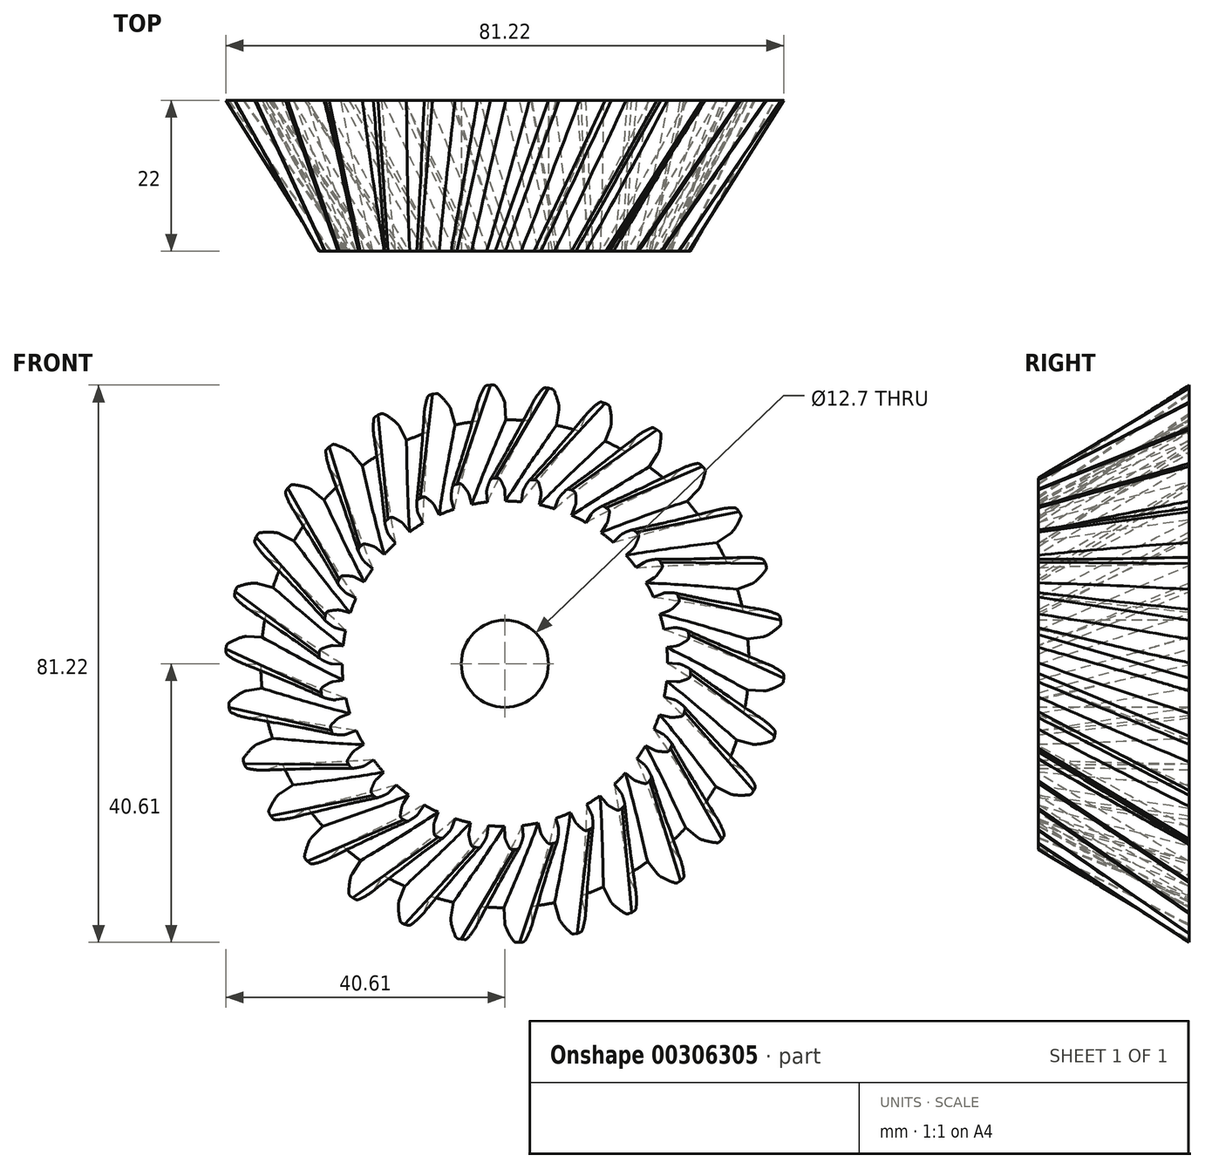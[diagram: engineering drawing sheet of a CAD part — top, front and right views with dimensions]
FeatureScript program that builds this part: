
annotation { "Feature Type Name" : "Feature", "Feature Type Description" : "" }
export const myFeature = defineFeature(function(context is Context, id is Id, definition is map)
    precondition{}
    {
        {
            var Q0;
            Q0=qCreatedBy(makeId("Front.planeOp"),FACE);
            var sketch = newSketch(context, id + "F0", { "sketchPlane" : qUnion([Q0])});
            skCircle(sketch, "E0", {"center": v(0, 0) * mm, "radius": 35.56 * mm});
            skPoint(sketch, "E1.endSnap0", {"position": v(-2, 38.15) * mm});
            skArc(sketch, "E2.trimOffspring", {"start": v(-0.1, 38.37) * mm, "mid": v(-0.63, 39.43) * mm, "end": v(-1.28, 40.41) * mm});
            skLineSegment(sketch, "E3", {"start": v(0.01, 37.84) * mm, "end": v(0.13, 35.56) * mm});
            skLineSegment(sketch, "E4", {"start": v(-1.68, 40.61) * mm, "end": v(-2.13, 40.61) * mm});
            skLineSegment(sketch, "E5.MirrorCS", {"start": v(-2.57, 40.57) * mm, "end": v(-2.13, 40.61) * mm});
            skArc(sketch, "E6.MirrorCS", {"start": v(-3.9, 38.17) * mm, "mid": v(-3.5, 39.27) * mm, "end": v(-2.96, 40.32) * mm});
            skLineSegment(sketch, "E7.MirrorCS", {"start": v(-3.97, 37.63) * mm, "end": v(-3.85, 35.35) * mm});
            skPoint(sketch, "E8.visualSharp", {"position": v(-2.82, 40.54) * mm});
            skArc(sketch, "E8.filletArc", {"start": v(-2.57, 40.57) * mm, "mid": v(-2.8, 40.5) * mm, "end": v(-2.96, 40.32) * mm});
            skPoint(sketch, "E9.visualSharp", {"position": v(-1.43, 40.61) * mm});
            skArc(sketch, "E9.filletArc", {"start": v(-1.28, 40.41) * mm, "mid": v(-1.45, 40.56) * mm, "end": v(-1.68, 40.61) * mm});
            skPoint(sketch, "E10.visualSharp", {"position": v(-3.98, 37.9) * mm});
            skArc(sketch, "E10.filletArc", {"start": v(-3.9, 38.17) * mm, "mid": v(-3.96, 37.9) * mm, "end": v(-3.97, 37.63) * mm});
            skPoint(sketch, "E11.visualSharp", {"position": v(0, 38.1) * mm});
            skArc(sketch, "E11.filletArc", {"start": v(0.01, 37.84) * mm, "mid": v(-0.02, 38.1) * mm, "end": v(-0.1, 38.37) * mm});
            skLineSegment(sketch, "E12.1.0", {"start": v(-11.7, 35.98) * mm, "end": v(-11.12, 33.78) * mm});
            skArc(sketch, "E12.1.1", {"start": v(-11.75, 36.52) * mm, "mid": v(-11.75, 36.25) * mm, "end": v(-11.7, 35.98) * mm});
            skArc(sketch, "E12.1.2", {"start": v(-11.75, 36.52) * mm, "mid": v(-11.59, 37.69) * mm, "end": v(-11.27, 38.83) * mm});
            skArc(sketch, "E12.1.3", {"start": v(-10.95, 39.15) * mm, "mid": v(-11.15, 39.03) * mm, "end": v(-11.27, 38.83) * mm});
            skLineSegment(sketch, "E12.1.4", {"start": v(-10.95, 39.15) * mm, "end": v(-10.53, 39.28) * mm});
            skLineSegment(sketch, "E12.1.5", {"start": v(-10.09, 39.38) * mm, "end": v(-10.53, 39.28) * mm});
            skArc(sketch, "E12.1.6", {"start": v(-9.65, 39.26) * mm, "mid": v(-9.86, 39.37) * mm, "end": v(-10.09, 39.38) * mm});
            skArc(sketch, "E12.1.7", {"start": v(-8.08, 37.5) * mm, "mid": v(-8.81, 38.43) * mm, "end": v(-9.65, 39.26) * mm});
            skArc(sketch, "E12.1.8", {"start": v(-7.85, 37.01) * mm, "mid": v(-7.95, 37.27) * mm, "end": v(-8.08, 37.5) * mm});
            skLineSegment(sketch, "E12.1.9", {"start": v(-7.85, 37.01) * mm, "end": v(-7.26, 34.81) * mm});
            skLineSegment(sketch, "E12.2.0", {"start": v(-18.93, 32.76) * mm, "end": v(-17.9, 30.73) * mm});
            skArc(sketch, "E12.2.1", {"start": v(-19.1, 33.28) * mm, "mid": v(-19.03, 33.01) * mm, "end": v(-18.93, 32.76) * mm});
            skArc(sketch, "E12.2.2", {"start": v(-19.1, 33.28) * mm, "mid": v(-19.17, 34.46) * mm, "end": v(-19.1, 35.64) * mm});
            skArc(sketch, "E12.2.3", {"start": v(-18.85, 36.01) * mm, "mid": v(-19.02, 35.85) * mm, "end": v(-19.1, 35.64) * mm});
            skLineSegment(sketch, "E12.2.4", {"start": v(-18.85, 36.01) * mm, "end": v(-18.46, 36.24) * mm});
            skLineSegment(sketch, "E12.2.5", {"start": v(-18.06, 36.42) * mm, "end": v(-18.46, 36.24) * mm});
            skArc(sketch, "E12.2.6", {"start": v(-17.6, 36.4) * mm, "mid": v(-17.83, 36.46) * mm, "end": v(-18.06, 36.42) * mm});
            skArc(sketch, "E12.2.7", {"start": v(-15.7, 35) * mm, "mid": v(-16.6, 35.76) * mm, "end": v(-17.6, 36.4) * mm});
            skArc(sketch, "E12.2.8", {"start": v(-15.38, 34.57) * mm, "mid": v(-15.52, 34.8) * mm, "end": v(-15.7, 35) * mm});
            skLineSegment(sketch, "E12.2.9", {"start": v(-15.38, 34.57) * mm, "end": v(-14.34, 32.54) * mm});
            skLineSegment(sketch, "E12.3.0", {"start": v(-25.33, 28.11) * mm, "end": v(-23.9, 26.34) * mm});
            skArc(sketch, "E12.3.1", {"start": v(-25.6, 28.58) * mm, "mid": v(-25.48, 28.34) * mm, "end": v(-25.33, 28.11) * mm});
            skArc(sketch, "E12.3.2", {"start": v(-25.6, 28.58) * mm, "mid": v(-25.91, 29.72) * mm, "end": v(-26.1, 30.88) * mm});
            skArc(sketch, "E12.3.3", {"start": v(-25.93, 31.3) * mm, "mid": v(-26.06, 31.12) * mm, "end": v(-26.1, 30.88) * mm});
            skLineSegment(sketch, "E12.3.4", {"start": v(-25.93, 31.3) * mm, "end": v(-25.6, 31.6) * mm});
            skLineSegment(sketch, "E12.3.5", {"start": v(-25.23, 31.87) * mm, "end": v(-25.6, 31.6) * mm});
            skArc(sketch, "E12.3.6", {"start": v(-24.79, 31.94) * mm, "mid": v(-25.02, 31.96) * mm, "end": v(-25.23, 31.87) * mm});
            skArc(sketch, "E12.3.7", {"start": v(-22.64, 30.98) * mm, "mid": v(-23.68, 31.53) * mm, "end": v(-24.79, 31.94) * mm});
            skArc(sketch, "E12.3.8", {"start": v(-22.23, 30.62) * mm, "mid": v(-22.42, 30.82) * mm, "end": v(-22.64, 30.98) * mm});
            skLineSegment(sketch, "E12.3.9", {"start": v(-22.23, 30.62) * mm, "end": v(-20.8, 28.85) * mm});
            skLineSegment(sketch, "E12.4.0", {"start": v(-30.62, 22.23) * mm, "end": v(-28.85, 20.8) * mm});
            skArc(sketch, "E12.4.1", {"start": v(-30.98, 22.64) * mm, "mid": v(-30.82, 22.42) * mm, "end": v(-30.62, 22.23) * mm});
            skArc(sketch, "E12.4.2", {"start": v(-30.98, 22.64) * mm, "mid": v(-31.53, 23.68) * mm, "end": v(-31.94, 24.79) * mm});
            skArc(sketch, "E12.4.3", {"start": v(-31.87, 25.23) * mm, "mid": v(-31.96, 25.02) * mm, "end": v(-31.94, 24.79) * mm});
            skLineSegment(sketch, "E12.4.4", {"start": v(-31.87, 25.23) * mm, "end": v(-31.6, 25.6) * mm});
            skLineSegment(sketch, "E12.4.5", {"start": v(-31.3, 25.93) * mm, "end": v(-31.6, 25.6) * mm});
            skArc(sketch, "E12.4.6", {"start": v(-30.88, 26.1) * mm, "mid": v(-31.12, 26.06) * mm, "end": v(-31.3, 25.93) * mm});
            skArc(sketch, "E12.4.7", {"start": v(-28.58, 25.6) * mm, "mid": v(-29.72, 25.91) * mm, "end": v(-30.88, 26.1) * mm});
            skArc(sketch, "E12.4.8", {"start": v(-28.11, 25.33) * mm, "mid": v(-28.34, 25.48) * mm, "end": v(-28.58, 25.6) * mm});
            skLineSegment(sketch, "E12.4.9", {"start": v(-28.11, 25.33) * mm, "end": v(-26.34, 23.9) * mm});
            skLineSegment(sketch, "E12.5.0", {"start": v(-34.57, 15.38) * mm, "end": v(-32.54, 14.34) * mm});
            skArc(sketch, "E12.5.1", {"start": v(-35, 15.7) * mm, "mid": v(-34.8, 15.52) * mm, "end": v(-34.57, 15.38) * mm});
            skArc(sketch, "E12.5.2", {"start": v(-35, 15.7) * mm, "mid": v(-35.76, 16.6) * mm, "end": v(-36.4, 17.6) * mm});
            skArc(sketch, "E12.5.3", {"start": v(-36.42, 18.06) * mm, "mid": v(-36.46, 17.83) * mm, "end": v(-36.4, 17.6) * mm});
            skLineSegment(sketch, "E12.5.4", {"start": v(-36.42, 18.06) * mm, "end": v(-36.24, 18.46) * mm});
            skLineSegment(sketch, "E12.5.5", {"start": v(-36.01, 18.85) * mm, "end": v(-36.24, 18.46) * mm});
            skArc(sketch, "E12.5.6", {"start": v(-35.64, 19.1) * mm, "mid": v(-35.85, 19.02) * mm, "end": v(-36.01, 18.85) * mm});
            skArc(sketch, "E12.5.7", {"start": v(-33.28, 19.1) * mm, "mid": v(-34.46, 19.17) * mm, "end": v(-35.64, 19.1) * mm});
            skArc(sketch, "E12.5.8", {"start": v(-32.76, 18.93) * mm, "mid": v(-33.01, 19.03) * mm, "end": v(-33.28, 19.1) * mm});
            skLineSegment(sketch, "E12.5.9", {"start": v(-32.76, 18.93) * mm, "end": v(-30.73, 17.9) * mm});
            skLineSegment(sketch, "E12.6.0", {"start": v(-37.01, 7.85) * mm, "end": v(-34.81, 7.26) * mm});
            skArc(sketch, "E12.6.1", {"start": v(-37.5, 8.08) * mm, "mid": v(-37.27, 7.95) * mm, "end": v(-37.01, 7.85) * mm});
            skArc(sketch, "E12.6.2", {"start": v(-37.5, 8.08) * mm, "mid": v(-38.43, 8.81) * mm, "end": v(-39.26, 9.65) * mm});
            skArc(sketch, "E12.6.3", {"start": v(-39.38, 10.09) * mm, "mid": v(-39.37, 9.86) * mm, "end": v(-39.26, 9.65) * mm});
            skLineSegment(sketch, "E12.6.4", {"start": v(-39.38, 10.09) * mm, "end": v(-39.28, 10.53) * mm});
            skLineSegment(sketch, "E12.6.5", {"start": v(-39.15, 10.95) * mm, "end": v(-39.28, 10.53) * mm});
            skArc(sketch, "E12.6.6", {"start": v(-38.83, 11.27) * mm, "mid": v(-39.03, 11.15) * mm, "end": v(-39.15, 10.95) * mm});
            skArc(sketch, "E12.6.7", {"start": v(-36.52, 11.75) * mm, "mid": v(-37.69, 11.59) * mm, "end": v(-38.83, 11.27) * mm});
            skArc(sketch, "E12.6.8", {"start": v(-35.98, 11.7) * mm, "mid": v(-36.25, 11.75) * mm, "end": v(-36.52, 11.75) * mm});
            skLineSegment(sketch, "E12.6.9", {"start": v(-35.98, 11.7) * mm, "end": v(-33.78, 11.12) * mm});
            skLineSegment(sketch, "E12.7.0", {"start": v(-37.84, -0.01) * mm, "end": v(-35.56, -0.13) * mm});
            skArc(sketch, "E12.7.1", {"start": v(-38.37, 0.1) * mm, "mid": v(-38.1, 0.02) * mm, "end": v(-37.84, -0.01) * mm});
            skArc(sketch, "E12.7.2", {"start": v(-38.37, 0.1) * mm, "mid": v(-39.43, 0.63) * mm, "end": v(-40.41, 1.28) * mm});
            skArc(sketch, "E12.7.3", {"start": v(-40.61, 1.68) * mm, "mid": v(-40.56, 1.45) * mm, "end": v(-40.41, 1.28) * mm});
            skLineSegment(sketch, "E12.7.4", {"start": v(-40.61, 1.68) * mm, "end": v(-40.61, 2.13) * mm});
            skLineSegment(sketch, "E12.7.5", {"start": v(-40.57, 2.57) * mm, "end": v(-40.61, 2.13) * mm});
            skArc(sketch, "E12.7.6", {"start": v(-40.32, 2.96) * mm, "mid": v(-40.5, 2.8) * mm, "end": v(-40.57, 2.57) * mm});
            skArc(sketch, "E12.7.7", {"start": v(-38.17, 3.9) * mm, "mid": v(-39.27, 3.5) * mm, "end": v(-40.32, 2.96) * mm});
            skArc(sketch, "E12.7.8", {"start": v(-37.63, 3.97) * mm, "mid": v(-37.9, 3.96) * mm, "end": v(-38.17, 3.9) * mm});
            skLineSegment(sketch, "E12.7.9", {"start": v(-37.63, 3.97) * mm, "end": v(-35.35, 3.85) * mm});
            skLineSegment(sketch, "E12.8.0", {"start": v(-37, -7.88) * mm, "end": v(-34.76, -7.52) * mm});
            skArc(sketch, "E12.8.1", {"start": v(-37.55, -7.87) * mm, "mid": v(-37.28, -7.9) * mm, "end": v(-37, -7.88) * mm});
            skArc(sketch, "E12.8.2", {"start": v(-37.55, -7.87) * mm, "mid": v(-38.7, -7.58) * mm, "end": v(-39.8, -7.15) * mm});
            skArc(sketch, "E12.8.3", {"start": v(-40.08, -6.8) * mm, "mid": v(-39.98, -7.01) * mm, "end": v(-39.8, -7.15) * mm});
            skLineSegment(sketch, "E12.8.4", {"start": v(-40.08, -6.8) * mm, "end": v(-40.17, -6.36) * mm});
            skLineSegment(sketch, "E12.8.5", {"start": v(-40.22, -5.92) * mm, "end": v(-40.17, -6.36) * mm});
            skArc(sketch, "E12.8.6", {"start": v(-40.06, -5.5) * mm, "mid": v(-40.19, -5.69) * mm, "end": v(-40.22, -5.92) * mm});
            skArc(sketch, "E12.8.7", {"start": v(-38.15, -4.12) * mm, "mid": v(-39.14, -4.75) * mm, "end": v(-40.06, -5.5) * mm});
            skArc(sketch, "E12.8.8", {"start": v(-37.63, -3.94) * mm, "mid": v(-37.9, -4) * mm, "end": v(-38.15, -4.12) * mm});
            skLineSegment(sketch, "E12.8.9", {"start": v(-37.63, -3.94) * mm, "end": v(-35.38, -3.58) * mm});
            skLineSegment(sketch, "E12.9.0", {"start": v(-34.56, -15.4) * mm, "end": v(-32.43, -14.59) * mm});
            skArc(sketch, "E12.9.1", {"start": v(-35.1, -15.5) * mm, "mid": v(-34.82, -15.48) * mm, "end": v(-34.56, -15.4) * mm});
            skArc(sketch, "E12.9.2", {"start": v(-35.1, -15.5) * mm, "mid": v(-36.27, -15.46) * mm, "end": v(-37.44, -15.27) * mm});
            skArc(sketch, "E12.9.3", {"start": v(-37.79, -14.98) * mm, "mid": v(-37.65, -15.17) * mm, "end": v(-37.44, -15.27) * mm});
            skLineSegment(sketch, "E12.9.4", {"start": v(-37.79, -14.98) * mm, "end": v(-37.97, -14.58) * mm});
            skLineSegment(sketch, "E12.9.5", {"start": v(-38.1, -14.15) * mm, "end": v(-37.97, -14.58) * mm});
            skArc(sketch, "E12.9.6", {"start": v(-38.04, -13.7) * mm, "mid": v(-38.13, -13.92) * mm, "end": v(-38.1, -14.15) * mm});
            skArc(sketch, "E12.9.7", {"start": v(-36.46, -11.96) * mm, "mid": v(-37.3, -12.78) * mm, "end": v(-38.04, -13.7) * mm});
            skArc(sketch, "E12.9.8", {"start": v(-36, -11.68) * mm, "mid": v(-36.24, -11.8) * mm, "end": v(-36.46, -11.96) * mm});
            skLineSegment(sketch, "E12.9.9", {"start": v(-36, -11.68) * mm, "end": v(-33.86, -10.86) * mm});
            skLineSegment(sketch, "E12.10.0", {"start": v(-30.6, -22.25) * mm, "end": v(-28.7, -21) * mm});
            skArc(sketch, "E12.10.1", {"start": v(-31.1, -22.47) * mm, "mid": v(-30.84, -22.38) * mm, "end": v(-30.6, -22.25) * mm});
            skArc(sketch, "E12.10.2", {"start": v(-31.1, -22.47) * mm, "mid": v(-32.26, -22.67) * mm, "end": v(-33.44, -22.72) * mm});
            skArc(sketch, "E12.10.3", {"start": v(-33.85, -22.51) * mm, "mid": v(-33.67, -22.66) * mm, "end": v(-33.44, -22.72) * mm});
            skLineSegment(sketch, "E12.10.4", {"start": v(-33.85, -22.51) * mm, "end": v(-34.1, -22.15) * mm});
            skLineSegment(sketch, "E12.10.5", {"start": v(-34.33, -21.76) * mm, "end": v(-34.1, -22.15) * mm});
            skArc(sketch, "E12.10.6", {"start": v(-34.36, -21.31) * mm, "mid": v(-34.4, -21.54) * mm, "end": v(-34.33, -21.76) * mm});
            skArc(sketch, "E12.10.7", {"start": v(-33.17, -19.28) * mm, "mid": v(-33.83, -20.26) * mm, "end": v(-34.36, -21.31) * mm});
            skArc(sketch, "E12.10.8", {"start": v(-32.78, -18.9) * mm, "mid": v(-33, -19.07) * mm, "end": v(-33.17, -19.28) * mm});
            skLineSegment(sketch, "E12.10.9", {"start": v(-32.78, -18.9) * mm, "end": v(-30.86, -17.66) * mm});
            skLineSegment(sketch, "E12.11.0", {"start": v(-25.3, -28.13) * mm, "end": v(-23.7, -26.52) * mm});
            skArc(sketch, "E12.11.1", {"start": v(-25.75, -28.44) * mm, "mid": v(-25.52, -28.3) * mm, "end": v(-25.3, -28.13) * mm});
            skArc(sketch, "E12.11.2", {"start": v(-25.75, -28.44) * mm, "mid": v(-26.85, -28.88) * mm, "end": v(-27.99, -29.18) * mm});
            skArc(sketch, "E12.11.3", {"start": v(-28.43, -29.06) * mm, "mid": v(-28.22, -29.17) * mm, "end": v(-27.99, -29.18) * mm});
            skLineSegment(sketch, "E12.11.4", {"start": v(-28.43, -29.06) * mm, "end": v(-28.76, -28.76) * mm});
            skLineSegment(sketch, "E12.11.5", {"start": v(-29.06, -28.43) * mm, "end": v(-28.76, -28.76) * mm});
            skArc(sketch, "E12.11.6", {"start": v(-29.18, -27.99) * mm, "mid": v(-29.17, -28.22) * mm, "end": v(-29.06, -28.43) * mm});
            skArc(sketch, "E12.11.7", {"start": v(-28.44, -25.75) * mm, "mid": v(-28.88, -26.85) * mm, "end": v(-29.18, -27.99) * mm});
            skArc(sketch, "E12.11.8", {"start": v(-28.13, -25.3) * mm, "mid": v(-28.3, -25.52) * mm, "end": v(-28.44, -25.75) * mm});
            skLineSegment(sketch, "E12.11.9", {"start": v(-28.13, -25.3) * mm, "end": v(-26.52, -23.7) * mm});
            skLineSegment(sketch, "E12.12.0", {"start": v(-18.9, -32.78) * mm, "end": v(-17.66, -30.86) * mm});
            skArc(sketch, "E12.12.1", {"start": v(-19.28, -33.17) * mm, "mid": v(-19.07, -33) * mm, "end": v(-18.9, -32.78) * mm});
            skArc(sketch, "E12.12.2", {"start": v(-19.28, -33.17) * mm, "mid": v(-20.26, -33.83) * mm, "end": v(-21.31, -34.36) * mm});
            skArc(sketch, "E12.12.3", {"start": v(-21.76, -34.33) * mm, "mid": v(-21.54, -34.4) * mm, "end": v(-21.31, -34.36) * mm});
            skLineSegment(sketch, "E12.12.4", {"start": v(-21.76, -34.33) * mm, "end": v(-22.15, -34.1) * mm});
            skLineSegment(sketch, "E12.12.5", {"start": v(-22.51, -33.85) * mm, "end": v(-22.15, -34.1) * mm});
            skArc(sketch, "E12.12.6", {"start": v(-22.72, -33.44) * mm, "mid": v(-22.66, -33.67) * mm, "end": v(-22.51, -33.85) * mm});
            skArc(sketch, "E12.12.7", {"start": v(-22.47, -31.1) * mm, "mid": v(-22.67, -32.26) * mm, "end": v(-22.72, -33.44) * mm});
            skArc(sketch, "E12.12.8", {"start": v(-22.25, -30.6) * mm, "mid": v(-22.38, -30.84) * mm, "end": v(-22.47, -31.1) * mm});
            skLineSegment(sketch, "E12.12.9", {"start": v(-22.25, -30.6) * mm, "end": v(-21, -28.7) * mm});
            skLineSegment(sketch, "E12.13.0", {"start": v(-11.68, -36) * mm, "end": v(-10.86, -33.86) * mm});
            skArc(sketch, "E12.13.1", {"start": v(-11.96, -36.46) * mm, "mid": v(-11.8, -36.24) * mm, "end": v(-11.68, -36) * mm});
            skArc(sketch, "E12.13.2", {"start": v(-11.96, -36.46) * mm, "mid": v(-12.78, -37.3) * mm, "end": v(-13.7, -38.04) * mm});
            skArc(sketch, "E12.13.3", {"start": v(-14.15, -38.1) * mm, "mid": v(-13.92, -38.13) * mm, "end": v(-13.7, -38.04) * mm});
            skLineSegment(sketch, "E12.13.4", {"start": v(-14.15, -38.1) * mm, "end": v(-14.58, -37.97) * mm});
            skLineSegment(sketch, "E12.13.5", {"start": v(-14.98, -37.79) * mm, "end": v(-14.58, -37.97) * mm});
            skArc(sketch, "E12.13.6", {"start": v(-15.27, -37.44) * mm, "mid": v(-15.17, -37.65) * mm, "end": v(-14.98, -37.79) * mm});
            skArc(sketch, "E12.13.7", {"start": v(-15.5, -35.1) * mm, "mid": v(-15.46, -36.27) * mm, "end": v(-15.27, -37.44) * mm});
            skArc(sketch, "E12.13.8", {"start": v(-15.4, -34.56) * mm, "mid": v(-15.48, -34.82) * mm, "end": v(-15.5, -35.1) * mm});
            skLineSegment(sketch, "E12.13.9", {"start": v(-15.4, -34.56) * mm, "end": v(-14.59, -32.43) * mm});
            skLineSegment(sketch, "E12.14.0", {"start": v(-3.94, -37.63) * mm, "end": v(-3.58, -35.38) * mm});
            skArc(sketch, "E12.14.1", {"start": v(-4.12, -38.15) * mm, "mid": v(-4, -37.9) * mm, "end": v(-3.94, -37.63) * mm});
            skArc(sketch, "E12.14.2", {"start": v(-4.12, -38.15) * mm, "mid": v(-4.75, -39.14) * mm, "end": v(-5.5, -40.06) * mm});
            skArc(sketch, "E12.14.3", {"start": v(-5.92, -40.22) * mm, "mid": v(-5.69, -40.19) * mm, "end": v(-5.5, -40.06) * mm});
            skLineSegment(sketch, "E12.14.4", {"start": v(-5.92, -40.22) * mm, "end": v(-6.36, -40.17) * mm});
            skLineSegment(sketch, "E12.14.5", {"start": v(-6.8, -40.08) * mm, "end": v(-6.36, -40.17) * mm});
            skArc(sketch, "E12.14.6", {"start": v(-7.15, -39.8) * mm, "mid": v(-7.01, -39.98) * mm, "end": v(-6.8, -40.08) * mm});
            skArc(sketch, "E12.14.7", {"start": v(-7.87, -37.55) * mm, "mid": v(-7.58, -38.7) * mm, "end": v(-7.15, -39.8) * mm});
            skArc(sketch, "E12.14.8", {"start": v(-7.88, -37) * mm, "mid": v(-7.9, -37.28) * mm, "end": v(-7.87, -37.55) * mm});
            skLineSegment(sketch, "E12.14.9", {"start": v(-7.88, -37) * mm, "end": v(-7.52, -34.76) * mm});
            skLineSegment(sketch, "E12.15.0", {"start": v(3.97, -37.63) * mm, "end": v(3.85, -35.35) * mm});
            skArc(sketch, "E12.15.1", {"start": v(3.9, -38.17) * mm, "mid": v(3.96, -37.9) * mm, "end": v(3.97, -37.63) * mm});
            skArc(sketch, "E12.15.2", {"start": v(3.9, -38.17) * mm, "mid": v(3.5, -39.27) * mm, "end": v(2.96, -40.32) * mm});
            skArc(sketch, "E12.15.3", {"start": v(2.57, -40.57) * mm, "mid": v(2.8, -40.5) * mm, "end": v(2.96, -40.32) * mm});
            skLineSegment(sketch, "E12.15.4", {"start": v(2.57, -40.57) * mm, "end": v(2.13, -40.61) * mm});
            skLineSegment(sketch, "E12.15.5", {"start": v(1.68, -40.61) * mm, "end": v(2.13, -40.61) * mm});
            skArc(sketch, "E12.15.6", {"start": v(1.28, -40.41) * mm, "mid": v(1.45, -40.56) * mm, "end": v(1.68, -40.61) * mm});
            skArc(sketch, "E12.15.7", {"start": v(0.1, -38.37) * mm, "mid": v(0.63, -39.43) * mm, "end": v(1.28, -40.41) * mm});
            skArc(sketch, "E12.15.8", {"start": v(-0.01, -37.84) * mm, "mid": v(0.02, -38.1) * mm, "end": v(0.1, -38.37) * mm});
            skLineSegment(sketch, "E12.15.9", {"start": v(-0.01, -37.84) * mm, "end": v(-0.13, -35.56) * mm});
            skLineSegment(sketch, "E12.16.0", {"start": v(11.7, -35.98) * mm, "end": v(11.12, -33.78) * mm});
            skArc(sketch, "E12.16.1", {"start": v(11.75, -36.52) * mm, "mid": v(11.75, -36.25) * mm, "end": v(11.7, -35.98) * mm});
            skArc(sketch, "E12.16.2", {"start": v(11.75, -36.52) * mm, "mid": v(11.59, -37.69) * mm, "end": v(11.27, -38.83) * mm});
            skArc(sketch, "E12.16.3", {"start": v(10.95, -39.15) * mm, "mid": v(11.15, -39.03) * mm, "end": v(11.27, -38.83) * mm});
            skLineSegment(sketch, "E12.16.4", {"start": v(10.95, -39.15) * mm, "end": v(10.53, -39.28) * mm});
            skLineSegment(sketch, "E12.16.5", {"start": v(10.09, -39.38) * mm, "end": v(10.53, -39.28) * mm});
            skArc(sketch, "E12.16.6", {"start": v(9.65, -39.26) * mm, "mid": v(9.86, -39.37) * mm, "end": v(10.09, -39.38) * mm});
            skArc(sketch, "E12.16.7", {"start": v(8.08, -37.5) * mm, "mid": v(8.81, -38.43) * mm, "end": v(9.65, -39.26) * mm});
            skArc(sketch, "E12.16.8", {"start": v(7.85, -37.01) * mm, "mid": v(7.95, -37.27) * mm, "end": v(8.08, -37.5) * mm});
            skLineSegment(sketch, "E12.16.9", {"start": v(7.85, -37.01) * mm, "end": v(7.26, -34.81) * mm});
            skLineSegment(sketch, "E12.17.0", {"start": v(18.93, -32.76) * mm, "end": v(17.9, -30.73) * mm});
            skArc(sketch, "E12.17.1", {"start": v(19.1, -33.28) * mm, "mid": v(19.03, -33.01) * mm, "end": v(18.93, -32.76) * mm});
            skArc(sketch, "E12.17.2", {"start": v(19.1, -33.28) * mm, "mid": v(19.17, -34.46) * mm, "end": v(19.1, -35.64) * mm});
            skArc(sketch, "E12.17.3", {"start": v(18.85, -36.01) * mm, "mid": v(19.02, -35.85) * mm, "end": v(19.1, -35.64) * mm});
            skLineSegment(sketch, "E12.17.4", {"start": v(18.85, -36.01) * mm, "end": v(18.46, -36.24) * mm});
            skLineSegment(sketch, "E12.17.5", {"start": v(18.06, -36.42) * mm, "end": v(18.46, -36.24) * mm});
            skArc(sketch, "E12.17.6", {"start": v(17.6, -36.4) * mm, "mid": v(17.83, -36.46) * mm, "end": v(18.06, -36.42) * mm});
            skArc(sketch, "E12.17.7", {"start": v(15.7, -35) * mm, "mid": v(16.6, -35.76) * mm, "end": v(17.6, -36.4) * mm});
            skArc(sketch, "E12.17.8", {"start": v(15.38, -34.57) * mm, "mid": v(15.52, -34.8) * mm, "end": v(15.7, -35) * mm});
            skLineSegment(sketch, "E12.17.9", {"start": v(15.38, -34.57) * mm, "end": v(14.34, -32.54) * mm});
            skLineSegment(sketch, "E12.18.0", {"start": v(25.33, -28.11) * mm, "end": v(23.9, -26.34) * mm});
            skArc(sketch, "E12.18.1", {"start": v(25.6, -28.58) * mm, "mid": v(25.48, -28.34) * mm, "end": v(25.33, -28.11) * mm});
            skArc(sketch, "E12.18.2", {"start": v(25.6, -28.58) * mm, "mid": v(25.91, -29.72) * mm, "end": v(26.1, -30.88) * mm});
            skArc(sketch, "E12.18.3", {"start": v(25.93, -31.3) * mm, "mid": v(26.06, -31.12) * mm, "end": v(26.1, -30.88) * mm});
            skLineSegment(sketch, "E12.18.4", {"start": v(25.93, -31.3) * mm, "end": v(25.6, -31.6) * mm});
            skLineSegment(sketch, "E12.18.5", {"start": v(25.23, -31.87) * mm, "end": v(25.6, -31.6) * mm});
            skArc(sketch, "E12.18.6", {"start": v(24.79, -31.94) * mm, "mid": v(25.02, -31.96) * mm, "end": v(25.23, -31.87) * mm});
            skArc(sketch, "E12.18.7", {"start": v(22.64, -30.98) * mm, "mid": v(23.68, -31.53) * mm, "end": v(24.79, -31.94) * mm});
            skArc(sketch, "E12.18.8", {"start": v(22.23, -30.62) * mm, "mid": v(22.42, -30.82) * mm, "end": v(22.64, -30.98) * mm});
            skLineSegment(sketch, "E12.18.9", {"start": v(22.23, -30.62) * mm, "end": v(20.8, -28.85) * mm});
            skLineSegment(sketch, "E12.19.0", {"start": v(30.62, -22.23) * mm, "end": v(28.85, -20.8) * mm});
            skArc(sketch, "E12.19.1", {"start": v(30.98, -22.64) * mm, "mid": v(30.82, -22.42) * mm, "end": v(30.62, -22.23) * mm});
            skArc(sketch, "E12.19.2", {"start": v(30.98, -22.64) * mm, "mid": v(31.53, -23.68) * mm, "end": v(31.94, -24.79) * mm});
            skArc(sketch, "E12.19.3", {"start": v(31.87, -25.23) * mm, "mid": v(31.96, -25.02) * mm, "end": v(31.94, -24.79) * mm});
            skLineSegment(sketch, "E12.19.4", {"start": v(31.87, -25.23) * mm, "end": v(31.6, -25.6) * mm});
            skLineSegment(sketch, "E12.19.5", {"start": v(31.3, -25.93) * mm, "end": v(31.6, -25.6) * mm});
            skArc(sketch, "E12.19.6", {"start": v(30.88, -26.1) * mm, "mid": v(31.12, -26.06) * mm, "end": v(31.3, -25.93) * mm});
            skArc(sketch, "E12.19.7", {"start": v(28.58, -25.6) * mm, "mid": v(29.72, -25.91) * mm, "end": v(30.88, -26.1) * mm});
            skArc(sketch, "E12.19.8", {"start": v(28.11, -25.33) * mm, "mid": v(28.34, -25.48) * mm, "end": v(28.58, -25.6) * mm});
            skLineSegment(sketch, "E12.19.9", {"start": v(28.11, -25.33) * mm, "end": v(26.34, -23.9) * mm});
            skLineSegment(sketch, "E12.20.0", {"start": v(34.57, -15.38) * mm, "end": v(32.54, -14.34) * mm});
            skArc(sketch, "E12.20.1", {"start": v(35, -15.7) * mm, "mid": v(34.8, -15.52) * mm, "end": v(34.57, -15.38) * mm});
            skArc(sketch, "E12.20.2", {"start": v(35, -15.7) * mm, "mid": v(35.76, -16.6) * mm, "end": v(36.4, -17.6) * mm});
            skArc(sketch, "E12.20.3", {"start": v(36.42, -18.06) * mm, "mid": v(36.46, -17.83) * mm, "end": v(36.4, -17.6) * mm});
            skLineSegment(sketch, "E12.20.4", {"start": v(36.42, -18.06) * mm, "end": v(36.24, -18.46) * mm});
            skLineSegment(sketch, "E12.20.5", {"start": v(36.01, -18.85) * mm, "end": v(36.24, -18.46) * mm});
            skArc(sketch, "E12.20.6", {"start": v(35.64, -19.1) * mm, "mid": v(35.85, -19.02) * mm, "end": v(36.01, -18.85) * mm});
            skArc(sketch, "E12.20.7", {"start": v(33.28, -19.1) * mm, "mid": v(34.46, -19.17) * mm, "end": v(35.64, -19.1) * mm});
            skArc(sketch, "E12.20.8", {"start": v(32.76, -18.93) * mm, "mid": v(33.01, -19.03) * mm, "end": v(33.28, -19.1) * mm});
            skLineSegment(sketch, "E12.20.9", {"start": v(32.76, -18.93) * mm, "end": v(30.73, -17.9) * mm});
            skLineSegment(sketch, "E12.21.0", {"start": v(37.01, -7.85) * mm, "end": v(34.81, -7.26) * mm});
            skArc(sketch, "E12.21.1", {"start": v(37.5, -8.08) * mm, "mid": v(37.27, -7.95) * mm, "end": v(37.01, -7.85) * mm});
            skArc(sketch, "E12.21.2", {"start": v(37.5, -8.08) * mm, "mid": v(38.43, -8.81) * mm, "end": v(39.26, -9.65) * mm});
            skArc(sketch, "E12.21.3", {"start": v(39.38, -10.09) * mm, "mid": v(39.37, -9.86) * mm, "end": v(39.26, -9.65) * mm});
            skLineSegment(sketch, "E12.21.4", {"start": v(39.38, -10.09) * mm, "end": v(39.28, -10.53) * mm});
            skLineSegment(sketch, "E12.21.5", {"start": v(39.15, -10.95) * mm, "end": v(39.28, -10.53) * mm});
            skArc(sketch, "E12.21.6", {"start": v(38.83, -11.27) * mm, "mid": v(39.03, -11.15) * mm, "end": v(39.15, -10.95) * mm});
            skArc(sketch, "E12.21.7", {"start": v(36.52, -11.75) * mm, "mid": v(37.69, -11.59) * mm, "end": v(38.83, -11.27) * mm});
            skArc(sketch, "E12.21.8", {"start": v(35.98, -11.7) * mm, "mid": v(36.25, -11.75) * mm, "end": v(36.52, -11.75) * mm});
            skLineSegment(sketch, "E12.21.9", {"start": v(35.98, -11.7) * mm, "end": v(33.78, -11.12) * mm});
            skLineSegment(sketch, "E12.22.0", {"start": v(37.84, 0.01) * mm, "end": v(35.56, 0.13) * mm});
            skArc(sketch, "E12.22.1", {"start": v(38.37, -0.1) * mm, "mid": v(38.1, -0.02) * mm, "end": v(37.84, 0.01) * mm});
            skArc(sketch, "E12.22.2", {"start": v(38.37, -0.1) * mm, "mid": v(39.43, -0.63) * mm, "end": v(40.41, -1.28) * mm});
            skArc(sketch, "E12.22.3", {"start": v(40.61, -1.68) * mm, "mid": v(40.56, -1.45) * mm, "end": v(40.41, -1.28) * mm});
            skLineSegment(sketch, "E12.22.4", {"start": v(40.61, -1.68) * mm, "end": v(40.61, -2.13) * mm});
            skLineSegment(sketch, "E12.22.5", {"start": v(40.57, -2.57) * mm, "end": v(40.61, -2.13) * mm});
            skArc(sketch, "E12.22.6", {"start": v(40.32, -2.96) * mm, "mid": v(40.5, -2.8) * mm, "end": v(40.57, -2.57) * mm});
            skArc(sketch, "E12.22.7", {"start": v(38.17, -3.9) * mm, "mid": v(39.27, -3.5) * mm, "end": v(40.32, -2.96) * mm});
            skArc(sketch, "E12.22.8", {"start": v(37.63, -3.97) * mm, "mid": v(37.9, -3.96) * mm, "end": v(38.17, -3.9) * mm});
            skLineSegment(sketch, "E12.22.9", {"start": v(37.63, -3.97) * mm, "end": v(35.35, -3.85) * mm});
            skLineSegment(sketch, "E12.23.0", {"start": v(37, 7.88) * mm, "end": v(34.76, 7.52) * mm});
            skArc(sketch, "E12.23.1", {"start": v(37.55, 7.87) * mm, "mid": v(37.28, 7.9) * mm, "end": v(37, 7.88) * mm});
            skArc(sketch, "E12.23.2", {"start": v(37.55, 7.87) * mm, "mid": v(38.7, 7.58) * mm, "end": v(39.8, 7.15) * mm});
            skArc(sketch, "E12.23.3", {"start": v(40.08, 6.8) * mm, "mid": v(39.98, 7.01) * mm, "end": v(39.8, 7.15) * mm});
            skLineSegment(sketch, "E12.23.4", {"start": v(40.08, 6.8) * mm, "end": v(40.17, 6.36) * mm});
            skLineSegment(sketch, "E12.23.5", {"start": v(40.22, 5.92) * mm, "end": v(40.17, 6.36) * mm});
            skArc(sketch, "E12.23.6", {"start": v(40.06, 5.5) * mm, "mid": v(40.19, 5.69) * mm, "end": v(40.22, 5.92) * mm});
            skArc(sketch, "E12.23.7", {"start": v(38.15, 4.12) * mm, "mid": v(39.14, 4.75) * mm, "end": v(40.06, 5.5) * mm});
            skArc(sketch, "E12.23.8", {"start": v(37.63, 3.94) * mm, "mid": v(37.9, 4) * mm, "end": v(38.15, 4.12) * mm});
            skLineSegment(sketch, "E12.23.9", {"start": v(37.63, 3.94) * mm, "end": v(35.38, 3.58) * mm});
            skLineSegment(sketch, "E12.24.0", {"start": v(34.56, 15.4) * mm, "end": v(32.43, 14.59) * mm});
            skArc(sketch, "E12.24.1", {"start": v(35.1, 15.5) * mm, "mid": v(34.82, 15.48) * mm, "end": v(34.56, 15.4) * mm});
            skArc(sketch, "E12.24.2", {"start": v(35.1, 15.5) * mm, "mid": v(36.27, 15.46) * mm, "end": v(37.44, 15.27) * mm});
            skArc(sketch, "E12.24.3", {"start": v(37.79, 14.98) * mm, "mid": v(37.65, 15.17) * mm, "end": v(37.44, 15.27) * mm});
            skLineSegment(sketch, "E12.24.4", {"start": v(37.79, 14.98) * mm, "end": v(37.97, 14.58) * mm});
            skLineSegment(sketch, "E12.24.5", {"start": v(38.1, 14.15) * mm, "end": v(37.97, 14.58) * mm});
            skArc(sketch, "E12.24.6", {"start": v(38.04, 13.7) * mm, "mid": v(38.13, 13.92) * mm, "end": v(38.1, 14.15) * mm});
            skArc(sketch, "E12.24.7", {"start": v(36.46, 11.96) * mm, "mid": v(37.3, 12.78) * mm, "end": v(38.04, 13.7) * mm});
            skArc(sketch, "E12.24.8", {"start": v(36, 11.68) * mm, "mid": v(36.24, 11.8) * mm, "end": v(36.46, 11.96) * mm});
            skLineSegment(sketch, "E12.24.9", {"start": v(36, 11.68) * mm, "end": v(33.86, 10.86) * mm});
            skLineSegment(sketch, "E12.25.0", {"start": v(30.6, 22.25) * mm, "end": v(28.7, 21) * mm});
            skArc(sketch, "E12.25.1", {"start": v(31.1, 22.47) * mm, "mid": v(30.84, 22.38) * mm, "end": v(30.6, 22.25) * mm});
            skArc(sketch, "E12.25.2", {"start": v(31.1, 22.47) * mm, "mid": v(32.26, 22.67) * mm, "end": v(33.44, 22.72) * mm});
            skArc(sketch, "E12.25.3", {"start": v(33.85, 22.51) * mm, "mid": v(33.67, 22.66) * mm, "end": v(33.44, 22.72) * mm});
            skLineSegment(sketch, "E12.25.4", {"start": v(33.85, 22.51) * mm, "end": v(34.1, 22.15) * mm});
            skLineSegment(sketch, "E12.25.5", {"start": v(34.33, 21.76) * mm, "end": v(34.1, 22.15) * mm});
            skArc(sketch, "E12.25.6", {"start": v(34.36, 21.31) * mm, "mid": v(34.4, 21.54) * mm, "end": v(34.33, 21.76) * mm});
            skArc(sketch, "E12.25.7", {"start": v(33.17, 19.28) * mm, "mid": v(33.83, 20.26) * mm, "end": v(34.36, 21.31) * mm});
            skArc(sketch, "E12.25.8", {"start": v(32.78, 18.9) * mm, "mid": v(33, 19.07) * mm, "end": v(33.17, 19.28) * mm});
            skLineSegment(sketch, "E12.25.9", {"start": v(32.78, 18.9) * mm, "end": v(30.86, 17.66) * mm});
            skLineSegment(sketch, "E12.26.0", {"start": v(25.3, 28.13) * mm, "end": v(23.7, 26.52) * mm});
            skArc(sketch, "E12.26.1", {"start": v(25.75, 28.44) * mm, "mid": v(25.52, 28.3) * mm, "end": v(25.3, 28.13) * mm});
            skArc(sketch, "E12.26.2", {"start": v(25.75, 28.44) * mm, "mid": v(26.85, 28.88) * mm, "end": v(27.99, 29.18) * mm});
            skArc(sketch, "E12.26.3", {"start": v(28.43, 29.06) * mm, "mid": v(28.22, 29.17) * mm, "end": v(27.99, 29.18) * mm});
            skLineSegment(sketch, "E12.26.4", {"start": v(28.43, 29.06) * mm, "end": v(28.76, 28.76) * mm});
            skLineSegment(sketch, "E12.26.5", {"start": v(29.06, 28.43) * mm, "end": v(28.76, 28.76) * mm});
            skArc(sketch, "E12.26.6", {"start": v(29.18, 27.99) * mm, "mid": v(29.17, 28.22) * mm, "end": v(29.06, 28.43) * mm});
            skArc(sketch, "E12.26.7", {"start": v(28.44, 25.75) * mm, "mid": v(28.88, 26.85) * mm, "end": v(29.18, 27.99) * mm});
            skArc(sketch, "E12.26.8", {"start": v(28.13, 25.3) * mm, "mid": v(28.3, 25.52) * mm, "end": v(28.44, 25.75) * mm});
            skLineSegment(sketch, "E12.26.9", {"start": v(28.13, 25.3) * mm, "end": v(26.52, 23.7) * mm});
            skLineSegment(sketch, "E12.27.0", {"start": v(18.9, 32.78) * mm, "end": v(17.66, 30.86) * mm});
            skArc(sketch, "E12.27.1", {"start": v(19.28, 33.17) * mm, "mid": v(19.07, 33) * mm, "end": v(18.9, 32.78) * mm});
            skArc(sketch, "E12.27.2", {"start": v(19.28, 33.17) * mm, "mid": v(20.26, 33.83) * mm, "end": v(21.31, 34.36) * mm});
            skArc(sketch, "E12.27.3", {"start": v(21.76, 34.33) * mm, "mid": v(21.54, 34.4) * mm, "end": v(21.31, 34.36) * mm});
            skLineSegment(sketch, "E12.27.4", {"start": v(21.76, 34.33) * mm, "end": v(22.15, 34.1) * mm});
            skLineSegment(sketch, "E12.27.5", {"start": v(22.51, 33.85) * mm, "end": v(22.15, 34.1) * mm});
            skArc(sketch, "E12.27.6", {"start": v(22.72, 33.44) * mm, "mid": v(22.66, 33.67) * mm, "end": v(22.51, 33.85) * mm});
            skArc(sketch, "E12.27.7", {"start": v(22.47, 31.1) * mm, "mid": v(22.67, 32.26) * mm, "end": v(22.72, 33.44) * mm});
            skArc(sketch, "E12.27.8", {"start": v(22.25, 30.6) * mm, "mid": v(22.38, 30.84) * mm, "end": v(22.47, 31.1) * mm});
            skLineSegment(sketch, "E12.27.9", {"start": v(22.25, 30.6) * mm, "end": v(21, 28.7) * mm});
            skLineSegment(sketch, "E12.28.0", {"start": v(11.68, 36) * mm, "end": v(10.86, 33.86) * mm});
            skArc(sketch, "E12.28.1", {"start": v(11.96, 36.46) * mm, "mid": v(11.8, 36.24) * mm, "end": v(11.68, 36) * mm});
            skArc(sketch, "E12.28.2", {"start": v(11.96, 36.46) * mm, "mid": v(12.78, 37.3) * mm, "end": v(13.7, 38.04) * mm});
            skArc(sketch, "E12.28.3", {"start": v(14.15, 38.1) * mm, "mid": v(13.92, 38.13) * mm, "end": v(13.7, 38.04) * mm});
            skLineSegment(sketch, "E12.28.4", {"start": v(14.15, 38.1) * mm, "end": v(14.58, 37.97) * mm});
            skLineSegment(sketch, "E12.28.5", {"start": v(14.98, 37.79) * mm, "end": v(14.58, 37.97) * mm});
            skArc(sketch, "E12.28.6", {"start": v(15.27, 37.44) * mm, "mid": v(15.17, 37.65) * mm, "end": v(14.98, 37.79) * mm});
            skArc(sketch, "E12.28.7", {"start": v(15.5, 35.1) * mm, "mid": v(15.46, 36.27) * mm, "end": v(15.27, 37.44) * mm});
            skArc(sketch, "E12.28.8", {"start": v(15.4, 34.56) * mm, "mid": v(15.48, 34.82) * mm, "end": v(15.5, 35.1) * mm});
            skLineSegment(sketch, "E12.28.9", {"start": v(15.4, 34.56) * mm, "end": v(14.59, 32.43) * mm});
            skLineSegment(sketch, "E12.29.0", {"start": v(3.94, 37.63) * mm, "end": v(3.58, 35.38) * mm});
            skArc(sketch, "E12.29.1", {"start": v(4.12, 38.15) * mm, "mid": v(4, 37.9) * mm, "end": v(3.94, 37.63) * mm});
            skArc(sketch, "E12.29.2", {"start": v(4.12, 38.15) * mm, "mid": v(4.75, 39.14) * mm, "end": v(5.5, 40.06) * mm});
            skArc(sketch, "E12.29.3", {"start": v(5.92, 40.22) * mm, "mid": v(5.69, 40.19) * mm, "end": v(5.5, 40.06) * mm});
            skLineSegment(sketch, "E12.29.4", {"start": v(5.92, 40.22) * mm, "end": v(6.36, 40.17) * mm});
            skLineSegment(sketch, "E12.29.5", {"start": v(6.8, 40.08) * mm, "end": v(6.36, 40.17) * mm});
            skArc(sketch, "E12.29.6", {"start": v(7.15, 39.8) * mm, "mid": v(7.01, 39.98) * mm, "end": v(6.8, 40.08) * mm});
            skArc(sketch, "E12.29.7", {"start": v(7.87, 37.55) * mm, "mid": v(7.58, 38.7) * mm, "end": v(7.15, 39.8) * mm});
            skArc(sketch, "E12.29.8", {"start": v(7.88, 37) * mm, "mid": v(7.9, 37.28) * mm, "end": v(7.87, 37.55) * mm});
            skLineSegment(sketch, "E12.29.9", {"start": v(7.88, 37) * mm, "end": v(7.52, 34.76) * mm});
            skSolve(sketch);
        }
        {
            var Q0;
            {var subQ0=sQuery(id+"F0.wireOp",EDGE,"E0");var subQ33=makeQuery(id+"F0.imprint","INTERSECT",VERTEX,{"derivedFrom":[subQ0,sQuery(id+"F0.wireOp",EDGE,"E12.22.0")]});Q0=makeQuery(id+"F0.imprint","IMPRINT",FACE,{"disambiguationData":[TD([[makeQuery(id+"F0.imprint","IMPRINT",EDGE,{"disambiguationData":[TD([[subQ33,-1.0]])],"derivedFrom":subQ0}),1.0]])]});}
            cPlane(context, id + "F1", {"entities" : qUnion([Q0]), "cplaneType" : CPlaneType.OFFSET, "offset" : 22 * mm, "width" : 152.4 * mm, "height" : 152.4 * mm});
        }
        {
            var Q0;
            Q0=qCreatedBy(id+"F1.planeOp",FACE);
            var sketch = newSketch(context, id + "F2", { "sketchPlane" : qUnion([Q0])});
            skCircle(sketch, "E13", {"center": v(0, 0) * mm, "radius": 23.71 * mm});
            skArc(sketch, "E14.trimOffspring", {"start": v(-0.1, 25.66) * mm, "mid": v(-0.36, 26.24) * mm, "end": v(-0.66, 26.81) * mm});
            skLineSegment(sketch, "E15", {"start": v(0.01, 25.15) * mm, "end": v(0.09, 23.71) * mm});
            skLineSegment(sketch, "E16", {"start": v(-1.11, 27.07) * mm, "end": v(-1.42, 27.06) * mm});
            skArc(sketch, "E17.MirrorCS", {"start": v(-2.58, 25.53) * mm, "mid": v(-2.39, 26.14) * mm, "end": v(-2.15, 26.73) * mm});
            skLineSegment(sketch, "E18.MirrorCS", {"start": v(-2.64, 25) * mm, "end": v(-2.57, 23.57) * mm});
            skLineSegment(sketch, "E19.MirrorCS", {"start": v(-1.72, 27.04) * mm, "end": v(-1.42, 27.06) * mm});
            skPoint(sketch, "E20.visualSharp", {"position": v(-2.02, 27.01) * mm});
            skArc(sketch, "E20.filletArc", {"start": v(-1.72, 27.04) * mm, "mid": v(-1.98, 26.94) * mm, "end": v(-2.15, 26.73) * mm});
            skPoint(sketch, "E21.visualSharp", {"position": v(-0.81, 27.08) * mm});
            skArc(sketch, "E21.filletArc", {"start": v(-0.66, 26.81) * mm, "mid": v(-0.85, 27) * mm, "end": v(-1.11, 27.07) * mm});
            skPoint(sketch, "E22.visualSharp", {"position": v(-2.66, 25.26) * mm});
            skArc(sketch, "E22.filletArc", {"start": v(-2.58, 25.53) * mm, "mid": v(-2.63, 25.27) * mm, "end": v(-2.64, 25) * mm});
            skPoint(sketch, "E23.visualSharp", {"position": v(0, 25.4) * mm});
            skArc(sketch, "E23.filletArc", {"start": v(0.01, 25.15) * mm, "mid": v(-0.02, 25.4) * mm, "end": v(-0.1, 25.66) * mm});
            skLineSegment(sketch, "E24.1.0", {"start": v(-7.78, 23.91) * mm, "end": v(-7.41, 22.52) * mm});
            skArc(sketch, "E24.1.1", {"start": v(-7.83, 24.43) * mm, "mid": v(-7.83, 24.17) * mm, "end": v(-7.78, 23.91) * mm});
            skArc(sketch, "E24.1.2", {"start": v(-7.83, 24.43) * mm, "mid": v(-7.77, 25.07) * mm, "end": v(-7.66, 25.7) * mm});
            skArc(sketch, "E24.1.3", {"start": v(-7.3, 26.09) * mm, "mid": v(-7.54, 25.94) * mm, "end": v(-7.66, 25.7) * mm});
            skLineSegment(sketch, "E24.1.4", {"start": v(-7.3, 26.09) * mm, "end": v(-7.01, 26.17) * mm});
            skLineSegment(sketch, "E24.1.5", {"start": v(-6.72, 26.25) * mm, "end": v(-7.01, 26.17) * mm});
            skArc(sketch, "E24.1.6", {"start": v(-6.22, 26.09) * mm, "mid": v(-6.44, 26.24) * mm, "end": v(-6.72, 26.25) * mm});
            skArc(sketch, "E24.1.7", {"start": v(-5.43, 25.08) * mm, "mid": v(-5.8, 25.6) * mm, "end": v(-6.22, 26.09) * mm});
            skArc(sketch, "E24.1.8", {"start": v(-5.22, 24.6) * mm, "mid": v(-5.3, 24.85) * mm, "end": v(-5.43, 25.08) * mm});
            skLineSegment(sketch, "E24.1.9", {"start": v(-5.22, 24.6) * mm, "end": v(-4.84, 23.21) * mm});
            skLineSegment(sketch, "E24.2.0", {"start": v(-12.59, 21.77) * mm, "end": v(-11.93, 20.49) * mm});
            skArc(sketch, "E24.2.1", {"start": v(-12.74, 22.27) * mm, "mid": v(-12.68, 22.01) * mm, "end": v(-12.59, 21.77) * mm});
            skArc(sketch, "E24.2.2", {"start": v(-12.74, 22.27) * mm, "mid": v(-12.81, 22.9) * mm, "end": v(-12.84, 23.55) * mm});
            skArc(sketch, "E24.2.3", {"start": v(-12.57, 24) * mm, "mid": v(-12.77, 23.8) * mm, "end": v(-12.84, 23.55) * mm});
            skLineSegment(sketch, "E24.2.4", {"start": v(-12.57, 24) * mm, "end": v(-12.3, 24.14) * mm});
            skLineSegment(sketch, "E24.2.5", {"start": v(-12.03, 24.28) * mm, "end": v(-12.3, 24.14) * mm});
            skArc(sketch, "E24.2.6", {"start": v(-11.5, 24.23) * mm, "mid": v(-11.76, 24.32) * mm, "end": v(-12.03, 24.28) * mm});
            skArc(sketch, "E24.2.7", {"start": v(-10.53, 23.4) * mm, "mid": v(-11, 23.83) * mm, "end": v(-11.5, 24.23) * mm});
            skArc(sketch, "E24.2.8", {"start": v(-10.22, 22.98) * mm, "mid": v(-10.35, 23.2) * mm, "end": v(-10.53, 23.4) * mm});
            skLineSegment(sketch, "E24.2.9", {"start": v(-10.22, 22.98) * mm, "end": v(-9.56, 21.7) * mm});
            skLineSegment(sketch, "E24.3.0", {"start": v(-16.84, 18.68) * mm, "end": v(-15.93, 17.56) * mm});
            skArc(sketch, "E24.3.1", {"start": v(-17.1, 19.13) * mm, "mid": v(-16.98, 18.9) * mm, "end": v(-16.84, 18.68) * mm});
            skArc(sketch, "E24.3.2", {"start": v(-17.1, 19.13) * mm, "mid": v(-17.3, 19.74) * mm, "end": v(-17.45, 20.36) * mm});
            skArc(sketch, "E24.3.3", {"start": v(-17.29, 20.86) * mm, "mid": v(-17.44, 20.63) * mm, "end": v(-17.45, 20.36) * mm});
            skLineSegment(sketch, "E24.3.4", {"start": v(-17.29, 20.86) * mm, "end": v(-17.05, 21.06) * mm});
            skLineSegment(sketch, "E24.3.5", {"start": v(-16.81, 21.24) * mm, "end": v(-17.05, 21.06) * mm});
            skArc(sketch, "E24.3.6", {"start": v(-16.29, 21.3) * mm, "mid": v(-16.56, 21.35) * mm, "end": v(-16.81, 21.24) * mm});
            skArc(sketch, "E24.3.7", {"start": v(-15.16, 20.7) * mm, "mid": v(-15.72, 21.02) * mm, "end": v(-16.29, 21.3) * mm});
            skArc(sketch, "E24.3.8", {"start": v(-14.77, 20.35) * mm, "mid": v(-14.95, 20.54) * mm, "end": v(-15.16, 20.7) * mm});
            skLineSegment(sketch, "E24.3.9", {"start": v(-14.77, 20.35) * mm, "end": v(-13.87, 19.23) * mm});
            skLineSegment(sketch, "E24.4.0", {"start": v(-20.35, 14.77) * mm, "end": v(-19.23, 13.87) * mm});
            skArc(sketch, "E24.4.1", {"start": v(-20.7, 15.16) * mm, "mid": v(-20.54, 14.95) * mm, "end": v(-20.35, 14.77) * mm});
            skArc(sketch, "E24.4.2", {"start": v(-20.7, 15.16) * mm, "mid": v(-21.02, 15.72) * mm, "end": v(-21.3, 16.29) * mm});
            skArc(sketch, "E24.4.3", {"start": v(-21.24, 16.81) * mm, "mid": v(-21.35, 16.56) * mm, "end": v(-21.3, 16.29) * mm});
            skLineSegment(sketch, "E24.4.4", {"start": v(-21.24, 16.81) * mm, "end": v(-21.06, 17.05) * mm});
            skLineSegment(sketch, "E24.4.5", {"start": v(-20.86, 17.29) * mm, "end": v(-21.06, 17.05) * mm});
            skArc(sketch, "E24.4.6", {"start": v(-20.36, 17.45) * mm, "mid": v(-20.63, 17.44) * mm, "end": v(-20.86, 17.29) * mm});
            skArc(sketch, "E24.4.7", {"start": v(-19.13, 17.1) * mm, "mid": v(-19.74, 17.3) * mm, "end": v(-20.36, 17.45) * mm});
            skArc(sketch, "E24.4.8", {"start": v(-18.68, 16.84) * mm, "mid": v(-18.9, 16.98) * mm, "end": v(-19.13, 17.1) * mm});
            skLineSegment(sketch, "E24.4.9", {"start": v(-18.68, 16.84) * mm, "end": v(-17.56, 15.93) * mm});
            skLineSegment(sketch, "E24.5.0", {"start": v(-22.98, 10.22) * mm, "end": v(-21.7, 9.56) * mm});
            skArc(sketch, "E24.5.1", {"start": v(-23.4, 10.53) * mm, "mid": v(-23.2, 10.35) * mm, "end": v(-22.98, 10.22) * mm});
            skArc(sketch, "E24.5.2", {"start": v(-23.4, 10.53) * mm, "mid": v(-23.83, 11) * mm, "end": v(-24.23, 11.5) * mm});
            skArc(sketch, "E24.5.3", {"start": v(-24.28, 12.03) * mm, "mid": v(-24.32, 11.76) * mm, "end": v(-24.23, 11.5) * mm});
            skLineSegment(sketch, "E24.5.4", {"start": v(-24.28, 12.03) * mm, "end": v(-24.14, 12.3) * mm});
            skLineSegment(sketch, "E24.5.5", {"start": v(-24, 12.57) * mm, "end": v(-24.14, 12.3) * mm});
            skArc(sketch, "E24.5.6", {"start": v(-23.55, 12.84) * mm, "mid": v(-23.8, 12.77) * mm, "end": v(-24, 12.57) * mm});
            skArc(sketch, "E24.5.7", {"start": v(-22.27, 12.74) * mm, "mid": v(-22.9, 12.81) * mm, "end": v(-23.55, 12.84) * mm});
            skArc(sketch, "E24.5.8", {"start": v(-21.77, 12.59) * mm, "mid": v(-22.01, 12.68) * mm, "end": v(-22.27, 12.74) * mm});
            skLineSegment(sketch, "E24.5.9", {"start": v(-21.77, 12.59) * mm, "end": v(-20.49, 11.93) * mm});
            skLineSegment(sketch, "E24.6.0", {"start": v(-24.6, 5.22) * mm, "end": v(-23.21, 4.84) * mm});
            skArc(sketch, "E24.6.1", {"start": v(-25.08, 5.43) * mm, "mid": v(-24.85, 5.3) * mm, "end": v(-24.6, 5.22) * mm});
            skArc(sketch, "E24.6.2", {"start": v(-25.08, 5.43) * mm, "mid": v(-25.6, 5.8) * mm, "end": v(-26.09, 6.22) * mm});
            skArc(sketch, "E24.6.3", {"start": v(-26.25, 6.72) * mm, "mid": v(-26.24, 6.44) * mm, "end": v(-26.09, 6.22) * mm});
            skLineSegment(sketch, "E24.6.4", {"start": v(-26.25, 6.72) * mm, "end": v(-26.17, 7.01) * mm});
            skLineSegment(sketch, "E24.6.5", {"start": v(-26.09, 7.3) * mm, "end": v(-26.17, 7.01) * mm});
            skArc(sketch, "E24.6.6", {"start": v(-25.7, 7.66) * mm, "mid": v(-25.94, 7.54) * mm, "end": v(-26.09, 7.3) * mm});
            skArc(sketch, "E24.6.7", {"start": v(-24.43, 7.83) * mm, "mid": v(-25.07, 7.77) * mm, "end": v(-25.7, 7.66) * mm});
            skArc(sketch, "E24.6.8", {"start": v(-23.91, 7.78) * mm, "mid": v(-24.17, 7.83) * mm, "end": v(-24.43, 7.83) * mm});
            skLineSegment(sketch, "E24.6.9", {"start": v(-23.91, 7.78) * mm, "end": v(-22.52, 7.41) * mm});
            skLineSegment(sketch, "E24.7.0", {"start": v(-25.15, -0.01) * mm, "end": v(-23.71, -0.09) * mm});
            skArc(sketch, "E24.7.1", {"start": v(-25.66, 0.1) * mm, "mid": v(-25.4, 0.02) * mm, "end": v(-25.15, -0.01) * mm});
            skArc(sketch, "E24.7.2", {"start": v(-25.66, 0.1) * mm, "mid": v(-26.24, 0.36) * mm, "end": v(-26.81, 0.66) * mm});
            skArc(sketch, "E24.7.3", {"start": v(-27.07, 1.11) * mm, "mid": v(-27, 0.85) * mm, "end": v(-26.81, 0.66) * mm});
            skLineSegment(sketch, "E24.7.4", {"start": v(-27.07, 1.11) * mm, "end": v(-27.06, 1.42) * mm});
            skLineSegment(sketch, "E24.7.5", {"start": v(-27.04, 1.72) * mm, "end": v(-27.06, 1.42) * mm});
            skArc(sketch, "E24.7.6", {"start": v(-26.73, 2.15) * mm, "mid": v(-26.94, 1.98) * mm, "end": v(-27.04, 1.72) * mm});
            skArc(sketch, "E24.7.7", {"start": v(-25.53, 2.58) * mm, "mid": v(-26.14, 2.39) * mm, "end": v(-26.73, 2.15) * mm});
            skArc(sketch, "E24.7.8", {"start": v(-25, 2.64) * mm, "mid": v(-25.27, 2.63) * mm, "end": v(-25.53, 2.58) * mm});
            skLineSegment(sketch, "E24.7.9", {"start": v(-25, 2.64) * mm, "end": v(-23.57, 2.57) * mm});
            skLineSegment(sketch, "E24.8.0", {"start": v(-24.6, -5.24) * mm, "end": v(-23.17, -5.02) * mm});
            skArc(sketch, "E24.8.1", {"start": v(-25.12, -5.24) * mm, "mid": v(-24.86, -5.26) * mm, "end": v(-24.6, -5.24) * mm});
            skArc(sketch, "E24.8.2", {"start": v(-25.12, -5.24) * mm, "mid": v(-25.74, -5.1) * mm, "end": v(-26.36, -4.93) * mm});
            skArc(sketch, "E24.8.3", {"start": v(-26.7, -4.54) * mm, "mid": v(-26.59, -4.78) * mm, "end": v(-26.36, -4.93) * mm});
            skLineSegment(sketch, "E24.8.4", {"start": v(-26.7, -4.54) * mm, "end": v(-26.76, -4.24) * mm});
            skLineSegment(sketch, "E24.8.5", {"start": v(-26.8, -3.94) * mm, "end": v(-26.76, -4.24) * mm});
            skArc(sketch, "E24.8.6", {"start": v(-26.6, -3.45) * mm, "mid": v(-26.77, -3.67) * mm, "end": v(-26.8, -3.94) * mm});
            skArc(sketch, "E24.8.7", {"start": v(-25.5, -2.78) * mm, "mid": v(-26.06, -3.1) * mm, "end": v(-26.6, -3.45) * mm});
            skArc(sketch, "E24.8.8", {"start": v(-25.01, -2.62) * mm, "mid": v(-25.27, -2.68) * mm, "end": v(-25.5, -2.78) * mm});
            skLineSegment(sketch, "E24.8.9", {"start": v(-25.01, -2.62) * mm, "end": v(-23.6, -2.4) * mm});
            skLineSegment(sketch, "E24.9.0", {"start": v(-22.97, -10.24) * mm, "end": v(-21.62, -9.72) * mm});
            skArc(sketch, "E24.9.1", {"start": v(-23.48, -10.35) * mm, "mid": v(-23.22, -10.31) * mm, "end": v(-22.97, -10.24) * mm});
            skArc(sketch, "E24.9.2", {"start": v(-23.48, -10.35) * mm, "mid": v(-24.12, -10.35) * mm, "end": v(-24.76, -10.3) * mm});
            skArc(sketch, "E24.9.3", {"start": v(-25.18, -10) * mm, "mid": v(-25.01, -10.2) * mm, "end": v(-24.76, -10.3) * mm});
            skLineSegment(sketch, "E24.9.4", {"start": v(-25.18, -10) * mm, "end": v(-25.3, -9.71) * mm});
            skLineSegment(sketch, "E24.9.5", {"start": v(-25.4, -9.42) * mm, "end": v(-25.3, -9.71) * mm});
            skArc(sketch, "E24.9.6", {"start": v(-25.3, -8.9) * mm, "mid": v(-25.42, -9.15) * mm, "end": v(-25.4, -9.42) * mm});
            skArc(sketch, "E24.9.7", {"start": v(-24.37, -8.02) * mm, "mid": v(-24.85, -8.45) * mm, "end": v(-25.3, -8.9) * mm});
            skArc(sketch, "E24.9.8", {"start": v(-23.92, -7.76) * mm, "mid": v(-24.16, -7.87) * mm, "end": v(-24.37, -8.02) * mm});
            skLineSegment(sketch, "E24.9.9", {"start": v(-23.92, -7.76) * mm, "end": v(-22.58, -7.24) * mm});
            skLineSegment(sketch, "E24.10.0", {"start": v(-20.34, -14.8) * mm, "end": v(-19.13, -14) * mm});
            skArc(sketch, "E24.10.1", {"start": v(-20.82, -15) * mm, "mid": v(-20.57, -14.92) * mm, "end": v(-20.34, -14.8) * mm});
            skArc(sketch, "E24.10.2", {"start": v(-20.82, -15) * mm, "mid": v(-21.44, -15.14) * mm, "end": v(-22.08, -15.23) * mm});
            skArc(sketch, "E24.10.3", {"start": v(-22.55, -15.01) * mm, "mid": v(-22.34, -15.19) * mm, "end": v(-22.08, -15.23) * mm});
            skLineSegment(sketch, "E24.10.4", {"start": v(-22.55, -15.01) * mm, "end": v(-22.72, -14.76) * mm});
            skLineSegment(sketch, "E24.10.5", {"start": v(-22.89, -14.5) * mm, "end": v(-22.72, -14.76) * mm});
            skArc(sketch, "E24.10.6", {"start": v(-22.9, -13.97) * mm, "mid": v(-22.96, -14.24) * mm, "end": v(-22.89, -14.5) * mm});
            skArc(sketch, "E24.10.7", {"start": v(-22.17, -12.91) * mm, "mid": v(-22.55, -13.43) * mm, "end": v(-22.9, -13.97) * mm});
            skArc(sketch, "E24.10.8", {"start": v(-21.79, -12.56) * mm, "mid": v(-22, -12.72) * mm, "end": v(-22.17, -12.91) * mm});
            skLineSegment(sketch, "E24.10.9", {"start": v(-21.79, -12.56) * mm, "end": v(-20.58, -11.78) * mm});
            skLineSegment(sketch, "E24.11.0", {"start": v(-16.82, -18.7) * mm, "end": v(-15.8, -17.68) * mm});
            skArc(sketch, "E24.11.1", {"start": v(-17.24, -19) * mm, "mid": v(-17.02, -18.87) * mm, "end": v(-16.82, -18.7) * mm});
            skArc(sketch, "E24.11.2", {"start": v(-17.24, -19) * mm, "mid": v(-17.83, -19.26) * mm, "end": v(-18.43, -19.49) * mm});
            skArc(sketch, "E24.11.3", {"start": v(-18.94, -19.37) * mm, "mid": v(-18.7, -19.5) * mm, "end": v(-18.43, -19.49) * mm});
            skLineSegment(sketch, "E24.11.4", {"start": v(-18.94, -19.37) * mm, "end": v(-19.16, -19.16) * mm});
            skLineSegment(sketch, "E24.11.5", {"start": v(-19.37, -18.94) * mm, "end": v(-19.16, -19.16) * mm});
            skArc(sketch, "E24.11.6", {"start": v(-19.49, -18.43) * mm, "mid": v(-19.5, -18.7) * mm, "end": v(-19.37, -18.94) * mm});
            skArc(sketch, "E24.11.7", {"start": v(-19, -17.24) * mm, "mid": v(-19.26, -17.83) * mm, "end": v(-19.49, -18.43) * mm});
            skArc(sketch, "E24.11.8", {"start": v(-18.7, -16.82) * mm, "mid": v(-18.87, -17.02) * mm, "end": v(-19, -17.24) * mm});
            skLineSegment(sketch, "E24.11.9", {"start": v(-18.7, -16.82) * mm, "end": v(-17.68, -15.8) * mm});
            skLineSegment(sketch, "E24.12.0", {"start": v(-12.56, -21.79) * mm, "end": v(-11.78, -20.58) * mm});
            skArc(sketch, "E24.12.1", {"start": v(-12.91, -22.17) * mm, "mid": v(-12.72, -22) * mm, "end": v(-12.56, -21.79) * mm});
            skArc(sketch, "E24.12.2", {"start": v(-12.91, -22.17) * mm, "mid": v(-13.43, -22.55) * mm, "end": v(-13.97, -22.9) * mm});
            skArc(sketch, "E24.12.3", {"start": v(-14.5, -22.89) * mm, "mid": v(-14.24, -22.96) * mm, "end": v(-13.97, -22.9) * mm});
            skLineSegment(sketch, "E24.12.4", {"start": v(-14.5, -22.89) * mm, "end": v(-14.76, -22.72) * mm});
            skLineSegment(sketch, "E24.12.5", {"start": v(-15.01, -22.55) * mm, "end": v(-14.76, -22.72) * mm});
            skArc(sketch, "E24.12.6", {"start": v(-15.23, -22.08) * mm, "mid": v(-15.19, -22.34) * mm, "end": v(-15.01, -22.55) * mm});
            skArc(sketch, "E24.12.7", {"start": v(-15, -20.82) * mm, "mid": v(-15.14, -21.44) * mm, "end": v(-15.23, -22.08) * mm});
            skArc(sketch, "E24.12.8", {"start": v(-14.8, -20.34) * mm, "mid": v(-14.92, -20.57) * mm, "end": v(-15, -20.82) * mm});
            skLineSegment(sketch, "E24.12.9", {"start": v(-14.8, -20.34) * mm, "end": v(-14, -19.13) * mm});
            skLineSegment(sketch, "E24.13.0", {"start": v(-7.76, -23.92) * mm, "end": v(-7.24, -22.58) * mm});
            skArc(sketch, "E24.13.1", {"start": v(-8.02, -24.37) * mm, "mid": v(-7.87, -24.16) * mm, "end": v(-7.76, -23.92) * mm});
            skArc(sketch, "E24.13.2", {"start": v(-8.02, -24.37) * mm, "mid": v(-8.45, -24.85) * mm, "end": v(-8.9, -25.3) * mm});
            skArc(sketch, "E24.13.3", {"start": v(-9.42, -25.4) * mm, "mid": v(-9.15, -25.42) * mm, "end": v(-8.9, -25.3) * mm});
            skLineSegment(sketch, "E24.13.4", {"start": v(-9.42, -25.4) * mm, "end": v(-9.71, -25.3) * mm});
            skLineSegment(sketch, "E24.13.5", {"start": v(-10, -25.18) * mm, "end": v(-9.71, -25.3) * mm});
            skArc(sketch, "E24.13.6", {"start": v(-10.3, -24.76) * mm, "mid": v(-10.2, -25.01) * mm, "end": v(-10, -25.18) * mm});
            skArc(sketch, "E24.13.7", {"start": v(-10.35, -23.48) * mm, "mid": v(-10.35, -24.12) * mm, "end": v(-10.3, -24.76) * mm});
            skArc(sketch, "E24.13.8", {"start": v(-10.24, -22.97) * mm, "mid": v(-10.31, -23.22) * mm, "end": v(-10.35, -23.48) * mm});
            skLineSegment(sketch, "E24.13.9", {"start": v(-10.24, -22.97) * mm, "end": v(-9.72, -21.62) * mm});
            skLineSegment(sketch, "E24.14.0", {"start": v(-2.62, -25.01) * mm, "end": v(-2.4, -23.6) * mm});
            skArc(sketch, "E24.14.1", {"start": v(-2.78, -25.5) * mm, "mid": v(-2.68, -25.27) * mm, "end": v(-2.62, -25.01) * mm});
            skArc(sketch, "E24.14.2", {"start": v(-2.78, -25.5) * mm, "mid": v(-3.1, -26.06) * mm, "end": v(-3.45, -26.6) * mm});
            skArc(sketch, "E24.14.3", {"start": v(-3.94, -26.8) * mm, "mid": v(-3.67, -26.77) * mm, "end": v(-3.45, -26.6) * mm});
            skLineSegment(sketch, "E24.14.4", {"start": v(-3.94, -26.8) * mm, "end": v(-4.24, -26.76) * mm});
            skLineSegment(sketch, "E24.14.5", {"start": v(-4.54, -26.7) * mm, "end": v(-4.24, -26.76) * mm});
            skArc(sketch, "E24.14.6", {"start": v(-4.93, -26.36) * mm, "mid": v(-4.78, -26.59) * mm, "end": v(-4.54, -26.7) * mm});
            skArc(sketch, "E24.14.7", {"start": v(-5.24, -25.12) * mm, "mid": v(-5.1, -25.74) * mm, "end": v(-4.93, -26.36) * mm});
            skArc(sketch, "E24.14.8", {"start": v(-5.24, -24.6) * mm, "mid": v(-5.26, -24.86) * mm, "end": v(-5.24, -25.12) * mm});
            skLineSegment(sketch, "E24.14.9", {"start": v(-5.24, -24.6) * mm, "end": v(-5.02, -23.17) * mm});
            skLineSegment(sketch, "E24.15.0", {"start": v(2.64, -25) * mm, "end": v(2.57, -23.57) * mm});
            skArc(sketch, "E24.15.1", {"start": v(2.58, -25.53) * mm, "mid": v(2.63, -25.27) * mm, "end": v(2.64, -25) * mm});
            skArc(sketch, "E24.15.2", {"start": v(2.58, -25.53) * mm, "mid": v(2.39, -26.14) * mm, "end": v(2.15, -26.73) * mm});
            skArc(sketch, "E24.15.3", {"start": v(1.72, -27.04) * mm, "mid": v(1.98, -26.94) * mm, "end": v(2.15, -26.73) * mm});
            skLineSegment(sketch, "E24.15.4", {"start": v(1.72, -27.04) * mm, "end": v(1.42, -27.06) * mm});
            skLineSegment(sketch, "E24.15.5", {"start": v(1.11, -27.07) * mm, "end": v(1.42, -27.06) * mm});
            skArc(sketch, "E24.15.6", {"start": v(0.66, -26.81) * mm, "mid": v(0.85, -27) * mm, "end": v(1.11, -27.07) * mm});
            skArc(sketch, "E24.15.7", {"start": v(0.1, -25.66) * mm, "mid": v(0.36, -26.24) * mm, "end": v(0.66, -26.81) * mm});
            skArc(sketch, "E24.15.8", {"start": v(-0.01, -25.15) * mm, "mid": v(0.02, -25.4) * mm, "end": v(0.1, -25.66) * mm});
            skLineSegment(sketch, "E24.15.9", {"start": v(-0.01, -25.15) * mm, "end": v(-0.09, -23.71) * mm});
            skLineSegment(sketch, "E24.16.0", {"start": v(7.78, -23.91) * mm, "end": v(7.41, -22.52) * mm});
            skArc(sketch, "E24.16.1", {"start": v(7.83, -24.43) * mm, "mid": v(7.83, -24.17) * mm, "end": v(7.78, -23.91) * mm});
            skArc(sketch, "E24.16.2", {"start": v(7.83, -24.43) * mm, "mid": v(7.77, -25.07) * mm, "end": v(7.66, -25.7) * mm});
            skArc(sketch, "E24.16.3", {"start": v(7.3, -26.09) * mm, "mid": v(7.54, -25.94) * mm, "end": v(7.66, -25.7) * mm});
            skLineSegment(sketch, "E24.16.4", {"start": v(7.3, -26.09) * mm, "end": v(7.01, -26.17) * mm});
            skLineSegment(sketch, "E24.16.5", {"start": v(6.72, -26.25) * mm, "end": v(7.01, -26.17) * mm});
            skArc(sketch, "E24.16.6", {"start": v(6.22, -26.09) * mm, "mid": v(6.44, -26.24) * mm, "end": v(6.72, -26.25) * mm});
            skArc(sketch, "E24.16.7", {"start": v(5.43, -25.08) * mm, "mid": v(5.8, -25.6) * mm, "end": v(6.22, -26.09) * mm});
            skArc(sketch, "E24.16.8", {"start": v(5.22, -24.6) * mm, "mid": v(5.3, -24.85) * mm, "end": v(5.43, -25.08) * mm});
            skLineSegment(sketch, "E24.16.9", {"start": v(5.22, -24.6) * mm, "end": v(4.84, -23.21) * mm});
            skLineSegment(sketch, "E24.17.0", {"start": v(12.59, -21.77) * mm, "end": v(11.93, -20.49) * mm});
            skArc(sketch, "E24.17.1", {"start": v(12.74, -22.27) * mm, "mid": v(12.68, -22.01) * mm, "end": v(12.59, -21.77) * mm});
            skArc(sketch, "E24.17.2", {"start": v(12.74, -22.27) * mm, "mid": v(12.81, -22.9) * mm, "end": v(12.84, -23.55) * mm});
            skArc(sketch, "E24.17.3", {"start": v(12.57, -24) * mm, "mid": v(12.77, -23.8) * mm, "end": v(12.84, -23.55) * mm});
            skLineSegment(sketch, "E24.17.4", {"start": v(12.57, -24) * mm, "end": v(12.3, -24.14) * mm});
            skLineSegment(sketch, "E24.17.5", {"start": v(12.03, -24.28) * mm, "end": v(12.3, -24.14) * mm});
            skArc(sketch, "E24.17.6", {"start": v(11.5, -24.23) * mm, "mid": v(11.76, -24.32) * mm, "end": v(12.03, -24.28) * mm});
            skArc(sketch, "E24.17.7", {"start": v(10.53, -23.4) * mm, "mid": v(11, -23.83) * mm, "end": v(11.5, -24.23) * mm});
            skArc(sketch, "E24.17.8", {"start": v(10.22, -22.98) * mm, "mid": v(10.35, -23.2) * mm, "end": v(10.53, -23.4) * mm});
            skLineSegment(sketch, "E24.17.9", {"start": v(10.22, -22.98) * mm, "end": v(9.56, -21.7) * mm});
            skLineSegment(sketch, "E24.18.0", {"start": v(16.84, -18.68) * mm, "end": v(15.93, -17.56) * mm});
            skArc(sketch, "E24.18.1", {"start": v(17.1, -19.13) * mm, "mid": v(16.98, -18.9) * mm, "end": v(16.84, -18.68) * mm});
            skArc(sketch, "E24.18.2", {"start": v(17.1, -19.13) * mm, "mid": v(17.3, -19.74) * mm, "end": v(17.45, -20.36) * mm});
            skArc(sketch, "E24.18.3", {"start": v(17.29, -20.86) * mm, "mid": v(17.44, -20.63) * mm, "end": v(17.45, -20.36) * mm});
            skLineSegment(sketch, "E24.18.4", {"start": v(17.29, -20.86) * mm, "end": v(17.05, -21.06) * mm});
            skLineSegment(sketch, "E24.18.5", {"start": v(16.81, -21.24) * mm, "end": v(17.05, -21.06) * mm});
            skArc(sketch, "E24.18.6", {"start": v(16.29, -21.3) * mm, "mid": v(16.56, -21.35) * mm, "end": v(16.81, -21.24) * mm});
            skArc(sketch, "E24.18.7", {"start": v(15.16, -20.7) * mm, "mid": v(15.72, -21.02) * mm, "end": v(16.29, -21.3) * mm});
            skArc(sketch, "E24.18.8", {"start": v(14.77, -20.35) * mm, "mid": v(14.95, -20.54) * mm, "end": v(15.16, -20.7) * mm});
            skLineSegment(sketch, "E24.18.9", {"start": v(14.77, -20.35) * mm, "end": v(13.87, -19.23) * mm});
            skLineSegment(sketch, "E24.19.0", {"start": v(20.35, -14.77) * mm, "end": v(19.23, -13.87) * mm});
            skArc(sketch, "E24.19.1", {"start": v(20.7, -15.16) * mm, "mid": v(20.54, -14.95) * mm, "end": v(20.35, -14.77) * mm});
            skArc(sketch, "E24.19.2", {"start": v(20.7, -15.16) * mm, "mid": v(21.02, -15.72) * mm, "end": v(21.3, -16.29) * mm});
            skArc(sketch, "E24.19.3", {"start": v(21.24, -16.81) * mm, "mid": v(21.35, -16.56) * mm, "end": v(21.3, -16.29) * mm});
            skLineSegment(sketch, "E24.19.4", {"start": v(21.24, -16.81) * mm, "end": v(21.06, -17.05) * mm});
            skLineSegment(sketch, "E24.19.5", {"start": v(20.86, -17.29) * mm, "end": v(21.06, -17.05) * mm});
            skArc(sketch, "E24.19.6", {"start": v(20.36, -17.45) * mm, "mid": v(20.63, -17.44) * mm, "end": v(20.86, -17.29) * mm});
            skArc(sketch, "E24.19.7", {"start": v(19.13, -17.1) * mm, "mid": v(19.74, -17.3) * mm, "end": v(20.36, -17.45) * mm});
            skArc(sketch, "E24.19.8", {"start": v(18.68, -16.84) * mm, "mid": v(18.9, -16.98) * mm, "end": v(19.13, -17.1) * mm});
            skLineSegment(sketch, "E24.19.9", {"start": v(18.68, -16.84) * mm, "end": v(17.56, -15.93) * mm});
            skLineSegment(sketch, "E24.20.0", {"start": v(22.98, -10.22) * mm, "end": v(21.7, -9.56) * mm});
            skArc(sketch, "E24.20.1", {"start": v(23.4, -10.53) * mm, "mid": v(23.2, -10.35) * mm, "end": v(22.98, -10.22) * mm});
            skArc(sketch, "E24.20.2", {"start": v(23.4, -10.53) * mm, "mid": v(23.83, -11) * mm, "end": v(24.23, -11.5) * mm});
            skArc(sketch, "E24.20.3", {"start": v(24.28, -12.03) * mm, "mid": v(24.32, -11.76) * mm, "end": v(24.23, -11.5) * mm});
            skLineSegment(sketch, "E24.20.4", {"start": v(24.28, -12.03) * mm, "end": v(24.14, -12.3) * mm});
            skLineSegment(sketch, "E24.20.5", {"start": v(24, -12.57) * mm, "end": v(24.14, -12.3) * mm});
            skArc(sketch, "E24.20.6", {"start": v(23.55, -12.84) * mm, "mid": v(23.8, -12.77) * mm, "end": v(24, -12.57) * mm});
            skArc(sketch, "E24.20.7", {"start": v(22.27, -12.74) * mm, "mid": v(22.9, -12.81) * mm, "end": v(23.55, -12.84) * mm});
            skArc(sketch, "E24.20.8", {"start": v(21.77, -12.59) * mm, "mid": v(22.01, -12.68) * mm, "end": v(22.27, -12.74) * mm});
            skLineSegment(sketch, "E24.20.9", {"start": v(21.77, -12.59) * mm, "end": v(20.49, -11.93) * mm});
            skLineSegment(sketch, "E24.21.0", {"start": v(24.6, -5.22) * mm, "end": v(23.21, -4.84) * mm});
            skArc(sketch, "E24.21.1", {"start": v(25.08, -5.43) * mm, "mid": v(24.85, -5.3) * mm, "end": v(24.6, -5.22) * mm});
            skArc(sketch, "E24.21.2", {"start": v(25.08, -5.43) * mm, "mid": v(25.6, -5.8) * mm, "end": v(26.09, -6.22) * mm});
            skArc(sketch, "E24.21.3", {"start": v(26.25, -6.72) * mm, "mid": v(26.24, -6.44) * mm, "end": v(26.09, -6.22) * mm});
            skLineSegment(sketch, "E24.21.4", {"start": v(26.25, -6.72) * mm, "end": v(26.17, -7.01) * mm});
            skLineSegment(sketch, "E24.21.5", {"start": v(26.09, -7.3) * mm, "end": v(26.17, -7.01) * mm});
            skArc(sketch, "E24.21.6", {"start": v(25.7, -7.66) * mm, "mid": v(25.94, -7.54) * mm, "end": v(26.09, -7.3) * mm});
            skArc(sketch, "E24.21.7", {"start": v(24.43, -7.83) * mm, "mid": v(25.07, -7.77) * mm, "end": v(25.7, -7.66) * mm});
            skArc(sketch, "E24.21.8", {"start": v(23.91, -7.78) * mm, "mid": v(24.17, -7.83) * mm, "end": v(24.43, -7.83) * mm});
            skLineSegment(sketch, "E24.21.9", {"start": v(23.91, -7.78) * mm, "end": v(22.52, -7.41) * mm});
            skLineSegment(sketch, "E24.22.0", {"start": v(25.15, 0.01) * mm, "end": v(23.71, 0.09) * mm});
            skArc(sketch, "E24.22.1", {"start": v(25.66, -0.1) * mm, "mid": v(25.4, -0.02) * mm, "end": v(25.15, 0.01) * mm});
            skArc(sketch, "E24.22.2", {"start": v(25.66, -0.1) * mm, "mid": v(26.24, -0.36) * mm, "end": v(26.81, -0.66) * mm});
            skArc(sketch, "E24.22.3", {"start": v(27.07, -1.11) * mm, "mid": v(27, -0.85) * mm, "end": v(26.81, -0.66) * mm});
            skLineSegment(sketch, "E24.22.4", {"start": v(27.07, -1.11) * mm, "end": v(27.06, -1.42) * mm});
            skLineSegment(sketch, "E24.22.5", {"start": v(27.04, -1.72) * mm, "end": v(27.06, -1.42) * mm});
            skArc(sketch, "E24.22.6", {"start": v(26.73, -2.15) * mm, "mid": v(26.94, -1.98) * mm, "end": v(27.04, -1.72) * mm});
            skArc(sketch, "E24.22.7", {"start": v(25.53, -2.58) * mm, "mid": v(26.14, -2.39) * mm, "end": v(26.73, -2.15) * mm});
            skArc(sketch, "E24.22.8", {"start": v(25, -2.64) * mm, "mid": v(25.27, -2.63) * mm, "end": v(25.53, -2.58) * mm});
            skLineSegment(sketch, "E24.22.9", {"start": v(25, -2.64) * mm, "end": v(23.57, -2.57) * mm});
            skLineSegment(sketch, "E24.23.0", {"start": v(24.6, 5.24) * mm, "end": v(23.17, 5.02) * mm});
            skArc(sketch, "E24.23.1", {"start": v(25.12, 5.24) * mm, "mid": v(24.86, 5.26) * mm, "end": v(24.6, 5.24) * mm});
            skArc(sketch, "E24.23.2", {"start": v(25.12, 5.24) * mm, "mid": v(25.74, 5.1) * mm, "end": v(26.36, 4.93) * mm});
            skArc(sketch, "E24.23.3", {"start": v(26.7, 4.54) * mm, "mid": v(26.59, 4.78) * mm, "end": v(26.36, 4.93) * mm});
            skLineSegment(sketch, "E24.23.4", {"start": v(26.7, 4.54) * mm, "end": v(26.76, 4.24) * mm});
            skLineSegment(sketch, "E24.23.5", {"start": v(26.8, 3.94) * mm, "end": v(26.76, 4.24) * mm});
            skArc(sketch, "E24.23.6", {"start": v(26.6, 3.45) * mm, "mid": v(26.77, 3.67) * mm, "end": v(26.8, 3.94) * mm});
            skArc(sketch, "E24.23.7", {"start": v(25.5, 2.78) * mm, "mid": v(26.06, 3.1) * mm, "end": v(26.6, 3.45) * mm});
            skArc(sketch, "E24.23.8", {"start": v(25.01, 2.62) * mm, "mid": v(25.27, 2.68) * mm, "end": v(25.5, 2.78) * mm});
            skLineSegment(sketch, "E24.23.9", {"start": v(25.01, 2.62) * mm, "end": v(23.6, 2.4) * mm});
            skLineSegment(sketch, "E24.24.0", {"start": v(22.97, 10.24) * mm, "end": v(21.62, 9.72) * mm});
            skArc(sketch, "E24.24.1", {"start": v(23.48, 10.35) * mm, "mid": v(23.22, 10.31) * mm, "end": v(22.97, 10.24) * mm});
            skArc(sketch, "E24.24.2", {"start": v(23.48, 10.35) * mm, "mid": v(24.12, 10.35) * mm, "end": v(24.76, 10.3) * mm});
            skArc(sketch, "E24.24.3", {"start": v(25.18, 10) * mm, "mid": v(25.01, 10.2) * mm, "end": v(24.76, 10.3) * mm});
            skLineSegment(sketch, "E24.24.4", {"start": v(25.18, 10) * mm, "end": v(25.3, 9.71) * mm});
            skLineSegment(sketch, "E24.24.5", {"start": v(25.4, 9.42) * mm, "end": v(25.3, 9.71) * mm});
            skArc(sketch, "E24.24.6", {"start": v(25.3, 8.9) * mm, "mid": v(25.42, 9.15) * mm, "end": v(25.4, 9.42) * mm});
            skArc(sketch, "E24.24.7", {"start": v(24.37, 8.02) * mm, "mid": v(24.85, 8.45) * mm, "end": v(25.3, 8.9) * mm});
            skArc(sketch, "E24.24.8", {"start": v(23.92, 7.76) * mm, "mid": v(24.16, 7.87) * mm, "end": v(24.37, 8.02) * mm});
            skLineSegment(sketch, "E24.24.9", {"start": v(23.92, 7.76) * mm, "end": v(22.58, 7.24) * mm});
            skLineSegment(sketch, "E24.25.0", {"start": v(20.34, 14.8) * mm, "end": v(19.13, 14) * mm});
            skArc(sketch, "E24.25.1", {"start": v(20.82, 15) * mm, "mid": v(20.57, 14.92) * mm, "end": v(20.34, 14.8) * mm});
            skArc(sketch, "E24.25.2", {"start": v(20.82, 15) * mm, "mid": v(21.44, 15.14) * mm, "end": v(22.08, 15.23) * mm});
            skArc(sketch, "E24.25.3", {"start": v(22.55, 15.01) * mm, "mid": v(22.34, 15.19) * mm, "end": v(22.08, 15.23) * mm});
            skLineSegment(sketch, "E24.25.4", {"start": v(22.55, 15.01) * mm, "end": v(22.72, 14.76) * mm});
            skLineSegment(sketch, "E24.25.5", {"start": v(22.89, 14.5) * mm, "end": v(22.72, 14.76) * mm});
            skArc(sketch, "E24.25.6", {"start": v(22.9, 13.97) * mm, "mid": v(22.96, 14.24) * mm, "end": v(22.89, 14.5) * mm});
            skArc(sketch, "E24.25.7", {"start": v(22.17, 12.91) * mm, "mid": v(22.55, 13.43) * mm, "end": v(22.9, 13.97) * mm});
            skArc(sketch, "E24.25.8", {"start": v(21.79, 12.56) * mm, "mid": v(22, 12.72) * mm, "end": v(22.17, 12.91) * mm});
            skLineSegment(sketch, "E24.25.9", {"start": v(21.79, 12.56) * mm, "end": v(20.58, 11.78) * mm});
            skLineSegment(sketch, "E24.26.0", {"start": v(16.82, 18.7) * mm, "end": v(15.8, 17.68) * mm});
            skArc(sketch, "E24.26.1", {"start": v(17.24, 19) * mm, "mid": v(17.02, 18.87) * mm, "end": v(16.82, 18.7) * mm});
            skArc(sketch, "E24.26.2", {"start": v(17.24, 19) * mm, "mid": v(17.83, 19.26) * mm, "end": v(18.43, 19.49) * mm});
            skArc(sketch, "E24.26.3", {"start": v(18.94, 19.37) * mm, "mid": v(18.7, 19.5) * mm, "end": v(18.43, 19.49) * mm});
            skLineSegment(sketch, "E24.26.4", {"start": v(18.94, 19.37) * mm, "end": v(19.16, 19.16) * mm});
            skLineSegment(sketch, "E24.26.5", {"start": v(19.37, 18.94) * mm, "end": v(19.16, 19.16) * mm});
            skArc(sketch, "E24.26.6", {"start": v(19.49, 18.43) * mm, "mid": v(19.5, 18.7) * mm, "end": v(19.37, 18.94) * mm});
            skArc(sketch, "E24.26.7", {"start": v(19, 17.24) * mm, "mid": v(19.26, 17.83) * mm, "end": v(19.49, 18.43) * mm});
            skArc(sketch, "E24.26.8", {"start": v(18.7, 16.82) * mm, "mid": v(18.87, 17.02) * mm, "end": v(19, 17.24) * mm});
            skLineSegment(sketch, "E24.26.9", {"start": v(18.7, 16.82) * mm, "end": v(17.68, 15.8) * mm});
            skLineSegment(sketch, "E24.27.0", {"start": v(12.56, 21.79) * mm, "end": v(11.78, 20.58) * mm});
            skArc(sketch, "E24.27.1", {"start": v(12.91, 22.17) * mm, "mid": v(12.72, 22) * mm, "end": v(12.56, 21.79) * mm});
            skArc(sketch, "E24.27.2", {"start": v(12.91, 22.17) * mm, "mid": v(13.43, 22.55) * mm, "end": v(13.97, 22.9) * mm});
            skArc(sketch, "E24.27.3", {"start": v(14.5, 22.89) * mm, "mid": v(14.24, 22.96) * mm, "end": v(13.97, 22.9) * mm});
            skLineSegment(sketch, "E24.27.4", {"start": v(14.5, 22.89) * mm, "end": v(14.76, 22.72) * mm});
            skLineSegment(sketch, "E24.27.5", {"start": v(15.01, 22.55) * mm, "end": v(14.76, 22.72) * mm});
            skArc(sketch, "E24.27.6", {"start": v(15.23, 22.08) * mm, "mid": v(15.19, 22.34) * mm, "end": v(15.01, 22.55) * mm});
            skArc(sketch, "E24.27.7", {"start": v(15, 20.82) * mm, "mid": v(15.14, 21.44) * mm, "end": v(15.23, 22.08) * mm});
            skArc(sketch, "E24.27.8", {"start": v(14.8, 20.34) * mm, "mid": v(14.92, 20.57) * mm, "end": v(15, 20.82) * mm});
            skLineSegment(sketch, "E24.27.9", {"start": v(14.8, 20.34) * mm, "end": v(14, 19.13) * mm});
            skLineSegment(sketch, "E24.28.0", {"start": v(7.76, 23.92) * mm, "end": v(7.24, 22.58) * mm});
            skArc(sketch, "E24.28.1", {"start": v(8.02, 24.37) * mm, "mid": v(7.87, 24.16) * mm, "end": v(7.76, 23.92) * mm});
            skArc(sketch, "E24.28.2", {"start": v(8.02, 24.37) * mm, "mid": v(8.45, 24.85) * mm, "end": v(8.9, 25.3) * mm});
            skArc(sketch, "E24.28.3", {"start": v(9.42, 25.4) * mm, "mid": v(9.15, 25.42) * mm, "end": v(8.9, 25.3) * mm});
            skLineSegment(sketch, "E24.28.4", {"start": v(9.42, 25.4) * mm, "end": v(9.71, 25.3) * mm});
            skLineSegment(sketch, "E24.28.5", {"start": v(10, 25.18) * mm, "end": v(9.71, 25.3) * mm});
            skArc(sketch, "E24.28.6", {"start": v(10.3, 24.76) * mm, "mid": v(10.2, 25.01) * mm, "end": v(10, 25.18) * mm});
            skArc(sketch, "E24.28.7", {"start": v(10.35, 23.48) * mm, "mid": v(10.35, 24.12) * mm, "end": v(10.3, 24.76) * mm});
            skArc(sketch, "E24.28.8", {"start": v(10.24, 22.97) * mm, "mid": v(10.31, 23.22) * mm, "end": v(10.35, 23.48) * mm});
            skLineSegment(sketch, "E24.28.9", {"start": v(10.24, 22.97) * mm, "end": v(9.72, 21.62) * mm});
            skLineSegment(sketch, "E24.29.0", {"start": v(2.62, 25.01) * mm, "end": v(2.4, 23.6) * mm});
            skArc(sketch, "E24.29.1", {"start": v(2.78, 25.5) * mm, "mid": v(2.68, 25.27) * mm, "end": v(2.62, 25.01) * mm});
            skArc(sketch, "E24.29.2", {"start": v(2.78, 25.5) * mm, "mid": v(3.1, 26.06) * mm, "end": v(3.45, 26.6) * mm});
            skArc(sketch, "E24.29.3", {"start": v(3.94, 26.8) * mm, "mid": v(3.67, 26.77) * mm, "end": v(3.45, 26.6) * mm});
            skLineSegment(sketch, "E24.29.4", {"start": v(3.94, 26.8) * mm, "end": v(4.24, 26.76) * mm});
            skLineSegment(sketch, "E24.29.5", {"start": v(4.54, 26.7) * mm, "end": v(4.24, 26.76) * mm});
            skArc(sketch, "E24.29.6", {"start": v(4.93, 26.36) * mm, "mid": v(4.78, 26.59) * mm, "end": v(4.54, 26.7) * mm});
            skArc(sketch, "E24.29.7", {"start": v(5.24, 25.12) * mm, "mid": v(5.1, 25.74) * mm, "end": v(4.93, 26.36) * mm});
            skArc(sketch, "E24.29.8", {"start": v(5.24, 24.6) * mm, "mid": v(5.26, 24.86) * mm, "end": v(5.24, 25.12) * mm});
            skLineSegment(sketch, "E24.29.9", {"start": v(5.24, 24.6) * mm, "end": v(5.02, 23.17) * mm});
            skSolve(sketch);
        }
        {
            var Q0;
            Q0=makeQuery(id+"F2.imprint","IMPRINT",FACE,{"disambiguationData":[TD([[makeQuery(id+"F2.imprint","IMPRINT",EDGE,{"derivedFrom":sQuery(id+"F2.wireOp",EDGE,"E14.trimOffspring")}),1.0]])]});
            var Q1;
            {var subQ0=sQuery(id+"F0.wireOp",EDGE,"E12.29.0");Q1=makeQuery(id+"F0.imprint","IMPRINT",FACE,{"disambiguationData":[TD([[makeQuery(id+"F0.imprint","IMPRINT",EDGE,{"derivedFrom":subQ0}),1.0]])]});}
            loft(context, id + "F3", {"sheetProfilesArray" : [{ "sheetProfileEntities" : qUnion([Q0]) }, { "sheetProfileEntities" : qUnion([Q1]) }]});
        }
        {
            var Q0;
            Q0=qCreatedBy(id+"F1.planeOp",FACE);
            var sketch = newSketch(context, id + "F4", { "sketchPlane" : qUnion([Q0])});
            skCircle(sketch, "E25", {"center": v(0, 0) * mm, "radius": 23.71 * mm});
            skSolve(sketch);
        }
        {
            var Q0;
            Q0=qCreatedBy(makeId("Front.planeOp"),FACE);
            var sketch = newSketch(context, id + "F5", { "sketchPlane" : qUnion([Q0])});
            skCircle(sketch, "E26", {"center": v(0, 0) * mm, "radius": 35.56 * mm});
            skSolve(sketch);
        }
        {
            var Q1;
            Q1=makeQuery(id+"F4.imprint","IMPRINT",FACE,{"disambiguationData":[TD([[makeQuery(id+"F4.imprint","IMPRINT",EDGE,{"derivedFrom":sQuery(id+"F4.wireOp",EDGE,"E25")}),1.0]])]});
            var Q2;
            Q2=makeQuery(id+"F5.imprint","IMPRINT",FACE,{"disambiguationData":[TD([[makeQuery(id+"F5.imprint","IMPRINT",EDGE,{"derivedFrom":sQuery(id+"F5.wireOp",EDGE,"E26")}),1.0]])]});
            loft(context, id + "F6", {"operationType" : NewBodyOperationType.ADD, "sheetProfilesArray" : [{ "sheetProfileEntities" : qUnion([Q1]) }, { "sheetProfileEntities" : qUnion([Q2]) }]});
        }
        {
            var Q0;
            {var subQ3=sQuery(id+"F0.wireOp",EDGE,"E12.29.0");Q0=makeQuery(id+"F3.opLoft","SWEPT_BODY",BODY,{"disambiguationData":[OSD([makeQuery(id+"F0.imprint","IMPRINT",FACE,{"disambiguationData":[TD([[makeQuery(id+"F0.imprint","IMPRINT",EDGE,{"derivedFrom":subQ3}),1.0]])]}),makeQuery(id+"F2.imprint","IMPRINT",FACE,{"disambiguationData":[TD([[makeQuery(id+"F2.imprint","IMPRINT",EDGE,{"derivedFrom":sQuery(id+"F2.wireOp",EDGE,"E14.trimOffspring")}),1.0]])]})])]});}
            var Q1;
            Q1=makeQuery(id+"F6.opLoft","SWEPT_FACE",FACE,{"disambiguationData":[OSD([sQuery(id+"F4.wireOp",EDGE,"E25"),sQuery(id+"F5.wireOp",EDGE,"E26")])]});
            circularPattern(context, id + "F7", {"entities" : qUnion([Q0]), "axis" : qUnion([Q1]), "angle" : 360 * degree, "instanceCount" : 30, "equalSpace" : true});
        }
        {
            var Q0;
            {var subQ3=sQuery(id+"F0.wireOp",EDGE,"E12.29.0");Q0=makeQuery(id+"F7.opPattern","COPY",BODY,{"derivedFrom":makeQuery(id+"F3.opLoft","SWEPT_BODY",BODY,{"disambiguationData":[OSD([makeQuery(id+"F0.imprint","IMPRINT",FACE,{"disambiguationData":[TD([[makeQuery(id+"F0.imprint","IMPRINT",EDGE,{"derivedFrom":subQ3}),1.0]])]}),makeQuery(id+"F2.imprint","IMPRINT",FACE,{"disambiguationData":[TD([[makeQuery(id+"F2.imprint","IMPRINT",EDGE,{"derivedFrom":sQuery(id+"F2.wireOp",EDGE,"E14.trimOffspring")}),1.0]])]})])]}),"instanceName":"11"});}
            var Q1;
            {var subQ3=sQuery(id+"F0.wireOp",EDGE,"E12.29.0");Q1=makeQuery(id+"F3.opLoft","SWEPT_BODY",BODY,{"disambiguationData":[OSD([makeQuery(id+"F0.imprint","IMPRINT",FACE,{"disambiguationData":[TD([[makeQuery(id+"F0.imprint","IMPRINT",EDGE,{"derivedFrom":subQ3}),1.0]])]}),makeQuery(id+"F2.imprint","IMPRINT",FACE,{"disambiguationData":[TD([[makeQuery(id+"F2.imprint","IMPRINT",EDGE,{"derivedFrom":sQuery(id+"F2.wireOp",EDGE,"E14.trimOffspring")}),1.0]])]})])]});}
            var Q2;
            {var subQ3=sQuery(id+"F0.wireOp",EDGE,"E12.29.0");Q2=makeQuery(id+"F7.opPattern","COPY",BODY,{"derivedFrom":makeQuery(id+"F3.opLoft","SWEPT_BODY",BODY,{"disambiguationData":[OSD([makeQuery(id+"F0.imprint","IMPRINT",FACE,{"disambiguationData":[TD([[makeQuery(id+"F0.imprint","IMPRINT",EDGE,{"derivedFrom":subQ3}),1.0]])]}),makeQuery(id+"F2.imprint","IMPRINT",FACE,{"disambiguationData":[TD([[makeQuery(id+"F2.imprint","IMPRINT",EDGE,{"derivedFrom":sQuery(id+"F2.wireOp",EDGE,"E14.trimOffspring")}),1.0]])]})])]}),"instanceName":"1"});}
            var Q3;
            {var subQ3=sQuery(id+"F0.wireOp",EDGE,"E12.29.0");Q3=makeQuery(id+"F7.opPattern","COPY",BODY,{"derivedFrom":makeQuery(id+"F3.opLoft","SWEPT_BODY",BODY,{"disambiguationData":[OSD([makeQuery(id+"F0.imprint","IMPRINT",FACE,{"disambiguationData":[TD([[makeQuery(id+"F0.imprint","IMPRINT",EDGE,{"derivedFrom":subQ3}),1.0]])]}),makeQuery(id+"F2.imprint","IMPRINT",FACE,{"disambiguationData":[TD([[makeQuery(id+"F2.imprint","IMPRINT",EDGE,{"derivedFrom":sQuery(id+"F2.wireOp",EDGE,"E14.trimOffspring")}),1.0]])]})])]}),"instanceName":"2"});}
            var Q4;
            {var subQ3=sQuery(id+"F0.wireOp",EDGE,"E12.29.0");Q4=makeQuery(id+"F7.opPattern","COPY",BODY,{"derivedFrom":makeQuery(id+"F3.opLoft","SWEPT_BODY",BODY,{"disambiguationData":[OSD([makeQuery(id+"F0.imprint","IMPRINT",FACE,{"disambiguationData":[TD([[makeQuery(id+"F0.imprint","IMPRINT",EDGE,{"derivedFrom":subQ3}),1.0]])]}),makeQuery(id+"F2.imprint","IMPRINT",FACE,{"disambiguationData":[TD([[makeQuery(id+"F2.imprint","IMPRINT",EDGE,{"derivedFrom":sQuery(id+"F2.wireOp",EDGE,"E14.trimOffspring")}),1.0]])]})])]}),"instanceName":"3"});}
            var Q5;
            {var subQ3=sQuery(id+"F0.wireOp",EDGE,"E12.29.0");Q5=makeQuery(id+"F7.opPattern","COPY",BODY,{"derivedFrom":makeQuery(id+"F3.opLoft","SWEPT_BODY",BODY,{"disambiguationData":[OSD([makeQuery(id+"F0.imprint","IMPRINT",FACE,{"disambiguationData":[TD([[makeQuery(id+"F0.imprint","IMPRINT",EDGE,{"derivedFrom":subQ3}),1.0]])]}),makeQuery(id+"F2.imprint","IMPRINT",FACE,{"disambiguationData":[TD([[makeQuery(id+"F2.imprint","IMPRINT",EDGE,{"derivedFrom":sQuery(id+"F2.wireOp",EDGE,"E14.trimOffspring")}),1.0]])]})])]}),"instanceName":"4"});}
            var Q6;
            {var subQ3=sQuery(id+"F0.wireOp",EDGE,"E12.29.0");Q6=makeQuery(id+"F7.opPattern","COPY",BODY,{"derivedFrom":makeQuery(id+"F3.opLoft","SWEPT_BODY",BODY,{"disambiguationData":[OSD([makeQuery(id+"F0.imprint","IMPRINT",FACE,{"disambiguationData":[TD([[makeQuery(id+"F0.imprint","IMPRINT",EDGE,{"derivedFrom":subQ3}),1.0]])]}),makeQuery(id+"F2.imprint","IMPRINT",FACE,{"disambiguationData":[TD([[makeQuery(id+"F2.imprint","IMPRINT",EDGE,{"derivedFrom":sQuery(id+"F2.wireOp",EDGE,"E14.trimOffspring")}),1.0]])]})])]}),"instanceName":"5"});}
            var Q7;
            {var subQ3=sQuery(id+"F0.wireOp",EDGE,"E12.29.0");Q7=makeQuery(id+"F7.opPattern","COPY",BODY,{"derivedFrom":makeQuery(id+"F3.opLoft","SWEPT_BODY",BODY,{"disambiguationData":[OSD([makeQuery(id+"F0.imprint","IMPRINT",FACE,{"disambiguationData":[TD([[makeQuery(id+"F0.imprint","IMPRINT",EDGE,{"derivedFrom":subQ3}),1.0]])]}),makeQuery(id+"F2.imprint","IMPRINT",FACE,{"disambiguationData":[TD([[makeQuery(id+"F2.imprint","IMPRINT",EDGE,{"derivedFrom":sQuery(id+"F2.wireOp",EDGE,"E14.trimOffspring")}),1.0]])]})])]}),"instanceName":"6"});}
            var Q8;
            {var subQ3=sQuery(id+"F0.wireOp",EDGE,"E12.29.0");Q8=makeQuery(id+"F7.opPattern","COPY",BODY,{"derivedFrom":makeQuery(id+"F3.opLoft","SWEPT_BODY",BODY,{"disambiguationData":[OSD([makeQuery(id+"F0.imprint","IMPRINT",FACE,{"disambiguationData":[TD([[makeQuery(id+"F0.imprint","IMPRINT",EDGE,{"derivedFrom":subQ3}),1.0]])]}),makeQuery(id+"F2.imprint","IMPRINT",FACE,{"disambiguationData":[TD([[makeQuery(id+"F2.imprint","IMPRINT",EDGE,{"derivedFrom":sQuery(id+"F2.wireOp",EDGE,"E14.trimOffspring")}),1.0]])]})])]}),"instanceName":"7"});}
            var Q9;
            {var subQ3=sQuery(id+"F0.wireOp",EDGE,"E12.29.0");Q9=makeQuery(id+"F7.opPattern","COPY",BODY,{"derivedFrom":makeQuery(id+"F3.opLoft","SWEPT_BODY",BODY,{"disambiguationData":[OSD([makeQuery(id+"F0.imprint","IMPRINT",FACE,{"disambiguationData":[TD([[makeQuery(id+"F0.imprint","IMPRINT",EDGE,{"derivedFrom":subQ3}),1.0]])]}),makeQuery(id+"F2.imprint","IMPRINT",FACE,{"disambiguationData":[TD([[makeQuery(id+"F2.imprint","IMPRINT",EDGE,{"derivedFrom":sQuery(id+"F2.wireOp",EDGE,"E14.trimOffspring")}),1.0]])]})])]}),"instanceName":"8"});}
            var Q10;
            {var subQ3=sQuery(id+"F0.wireOp",EDGE,"E12.29.0");Q10=makeQuery(id+"F7.opPattern","COPY",BODY,{"derivedFrom":makeQuery(id+"F3.opLoft","SWEPT_BODY",BODY,{"disambiguationData":[OSD([makeQuery(id+"F0.imprint","IMPRINT",FACE,{"disambiguationData":[TD([[makeQuery(id+"F0.imprint","IMPRINT",EDGE,{"derivedFrom":subQ3}),1.0]])]}),makeQuery(id+"F2.imprint","IMPRINT",FACE,{"disambiguationData":[TD([[makeQuery(id+"F2.imprint","IMPRINT",EDGE,{"derivedFrom":sQuery(id+"F2.wireOp",EDGE,"E14.trimOffspring")}),1.0]])]})])]}),"instanceName":"9"});}
            var Q11;
            {var subQ3=sQuery(id+"F0.wireOp",EDGE,"E12.29.0");Q11=makeQuery(id+"F7.opPattern","COPY",BODY,{"derivedFrom":makeQuery(id+"F3.opLoft","SWEPT_BODY",BODY,{"disambiguationData":[OSD([makeQuery(id+"F0.imprint","IMPRINT",FACE,{"disambiguationData":[TD([[makeQuery(id+"F0.imprint","IMPRINT",EDGE,{"derivedFrom":subQ3}),1.0]])]}),makeQuery(id+"F2.imprint","IMPRINT",FACE,{"disambiguationData":[TD([[makeQuery(id+"F2.imprint","IMPRINT",EDGE,{"derivedFrom":sQuery(id+"F2.wireOp",EDGE,"E14.trimOffspring")}),1.0]])]})])]}),"instanceName":"10"});}
            var Q12;
            {var subQ3=sQuery(id+"F0.wireOp",EDGE,"E12.29.0");Q12=makeQuery(id+"F7.opPattern","COPY",BODY,{"derivedFrom":makeQuery(id+"F3.opLoft","SWEPT_BODY",BODY,{"disambiguationData":[OSD([makeQuery(id+"F0.imprint","IMPRINT",FACE,{"disambiguationData":[TD([[makeQuery(id+"F0.imprint","IMPRINT",EDGE,{"derivedFrom":subQ3}),1.0]])]}),makeQuery(id+"F2.imprint","IMPRINT",FACE,{"disambiguationData":[TD([[makeQuery(id+"F2.imprint","IMPRINT",EDGE,{"derivedFrom":sQuery(id+"F2.wireOp",EDGE,"E14.trimOffspring")}),1.0]])]})])]}),"instanceName":"29"});}
            var Q13;
            {var subQ3=sQuery(id+"F0.wireOp",EDGE,"E12.29.0");Q13=makeQuery(id+"F7.opPattern","COPY",BODY,{"derivedFrom":makeQuery(id+"F3.opLoft","SWEPT_BODY",BODY,{"disambiguationData":[OSD([makeQuery(id+"F0.imprint","IMPRINT",FACE,{"disambiguationData":[TD([[makeQuery(id+"F0.imprint","IMPRINT",EDGE,{"derivedFrom":subQ3}),1.0]])]}),makeQuery(id+"F2.imprint","IMPRINT",FACE,{"disambiguationData":[TD([[makeQuery(id+"F2.imprint","IMPRINT",EDGE,{"derivedFrom":sQuery(id+"F2.wireOp",EDGE,"E14.trimOffspring")}),1.0]])]})])]}),"instanceName":"28"});}
            var Q14;
            {var subQ3=sQuery(id+"F0.wireOp",EDGE,"E12.29.0");Q14=makeQuery(id+"F7.opPattern","COPY",BODY,{"derivedFrom":makeQuery(id+"F3.opLoft","SWEPT_BODY",BODY,{"disambiguationData":[OSD([makeQuery(id+"F0.imprint","IMPRINT",FACE,{"disambiguationData":[TD([[makeQuery(id+"F0.imprint","IMPRINT",EDGE,{"derivedFrom":subQ3}),1.0]])]}),makeQuery(id+"F2.imprint","IMPRINT",FACE,{"disambiguationData":[TD([[makeQuery(id+"F2.imprint","IMPRINT",EDGE,{"derivedFrom":sQuery(id+"F2.wireOp",EDGE,"E14.trimOffspring")}),1.0]])]})])]}),"instanceName":"27"});}
            var Q15;
            {var subQ3=sQuery(id+"F0.wireOp",EDGE,"E12.29.0");Q15=makeQuery(id+"F7.opPattern","COPY",BODY,{"derivedFrom":makeQuery(id+"F3.opLoft","SWEPT_BODY",BODY,{"disambiguationData":[OSD([makeQuery(id+"F0.imprint","IMPRINT",FACE,{"disambiguationData":[TD([[makeQuery(id+"F0.imprint","IMPRINT",EDGE,{"derivedFrom":subQ3}),1.0]])]}),makeQuery(id+"F2.imprint","IMPRINT",FACE,{"disambiguationData":[TD([[makeQuery(id+"F2.imprint","IMPRINT",EDGE,{"derivedFrom":sQuery(id+"F2.wireOp",EDGE,"E14.trimOffspring")}),1.0]])]})])]}),"instanceName":"26"});}
            var Q16;
            {var subQ3=sQuery(id+"F0.wireOp",EDGE,"E12.29.0");Q16=makeQuery(id+"F7.opPattern","COPY",BODY,{"derivedFrom":makeQuery(id+"F3.opLoft","SWEPT_BODY",BODY,{"disambiguationData":[OSD([makeQuery(id+"F0.imprint","IMPRINT",FACE,{"disambiguationData":[TD([[makeQuery(id+"F0.imprint","IMPRINT",EDGE,{"derivedFrom":subQ3}),1.0]])]}),makeQuery(id+"F2.imprint","IMPRINT",FACE,{"disambiguationData":[TD([[makeQuery(id+"F2.imprint","IMPRINT",EDGE,{"derivedFrom":sQuery(id+"F2.wireOp",EDGE,"E14.trimOffspring")}),1.0]])]})])]}),"instanceName":"25"});}
            var Q17;
            {var subQ3=sQuery(id+"F0.wireOp",EDGE,"E12.29.0");Q17=makeQuery(id+"F7.opPattern","COPY",BODY,{"derivedFrom":makeQuery(id+"F3.opLoft","SWEPT_BODY",BODY,{"disambiguationData":[OSD([makeQuery(id+"F0.imprint","IMPRINT",FACE,{"disambiguationData":[TD([[makeQuery(id+"F0.imprint","IMPRINT",EDGE,{"derivedFrom":subQ3}),1.0]])]}),makeQuery(id+"F2.imprint","IMPRINT",FACE,{"disambiguationData":[TD([[makeQuery(id+"F2.imprint","IMPRINT",EDGE,{"derivedFrom":sQuery(id+"F2.wireOp",EDGE,"E14.trimOffspring")}),1.0]])]})])]}),"instanceName":"24"});}
            var Q18;
            {var subQ3=sQuery(id+"F0.wireOp",EDGE,"E12.29.0");Q18=makeQuery(id+"F7.opPattern","COPY",BODY,{"derivedFrom":makeQuery(id+"F3.opLoft","SWEPT_BODY",BODY,{"disambiguationData":[OSD([makeQuery(id+"F0.imprint","IMPRINT",FACE,{"disambiguationData":[TD([[makeQuery(id+"F0.imprint","IMPRINT",EDGE,{"derivedFrom":subQ3}),1.0]])]}),makeQuery(id+"F2.imprint","IMPRINT",FACE,{"disambiguationData":[TD([[makeQuery(id+"F2.imprint","IMPRINT",EDGE,{"derivedFrom":sQuery(id+"F2.wireOp",EDGE,"E14.trimOffspring")}),1.0]])]})])]}),"instanceName":"23"});}
            var Q19;
            {var subQ3=sQuery(id+"F0.wireOp",EDGE,"E12.29.0");Q19=makeQuery(id+"F7.opPattern","COPY",BODY,{"derivedFrom":makeQuery(id+"F3.opLoft","SWEPT_BODY",BODY,{"disambiguationData":[OSD([makeQuery(id+"F0.imprint","IMPRINT",FACE,{"disambiguationData":[TD([[makeQuery(id+"F0.imprint","IMPRINT",EDGE,{"derivedFrom":subQ3}),1.0]])]}),makeQuery(id+"F2.imprint","IMPRINT",FACE,{"disambiguationData":[TD([[makeQuery(id+"F2.imprint","IMPRINT",EDGE,{"derivedFrom":sQuery(id+"F2.wireOp",EDGE,"E14.trimOffspring")}),1.0]])]})])]}),"instanceName":"22"});}
            var Q20;
            {var subQ3=sQuery(id+"F0.wireOp",EDGE,"E12.29.0");Q20=makeQuery(id+"F7.opPattern","COPY",BODY,{"derivedFrom":makeQuery(id+"F3.opLoft","SWEPT_BODY",BODY,{"disambiguationData":[OSD([makeQuery(id+"F0.imprint","IMPRINT",FACE,{"disambiguationData":[TD([[makeQuery(id+"F0.imprint","IMPRINT",EDGE,{"derivedFrom":subQ3}),1.0]])]}),makeQuery(id+"F2.imprint","IMPRINT",FACE,{"disambiguationData":[TD([[makeQuery(id+"F2.imprint","IMPRINT",EDGE,{"derivedFrom":sQuery(id+"F2.wireOp",EDGE,"E14.trimOffspring")}),1.0]])]})])]}),"instanceName":"21"});}
            var Q21;
            {var subQ3=sQuery(id+"F0.wireOp",EDGE,"E12.29.0");Q21=makeQuery(id+"F7.opPattern","COPY",BODY,{"derivedFrom":makeQuery(id+"F3.opLoft","SWEPT_BODY",BODY,{"disambiguationData":[OSD([makeQuery(id+"F0.imprint","IMPRINT",FACE,{"disambiguationData":[TD([[makeQuery(id+"F0.imprint","IMPRINT",EDGE,{"derivedFrom":subQ3}),1.0]])]}),makeQuery(id+"F2.imprint","IMPRINT",FACE,{"disambiguationData":[TD([[makeQuery(id+"F2.imprint","IMPRINT",EDGE,{"derivedFrom":sQuery(id+"F2.wireOp",EDGE,"E14.trimOffspring")}),1.0]])]})])]}),"instanceName":"20"});}
            var Q22;
            {var subQ3=sQuery(id+"F0.wireOp",EDGE,"E12.29.0");Q22=makeQuery(id+"F7.opPattern","COPY",BODY,{"derivedFrom":makeQuery(id+"F3.opLoft","SWEPT_BODY",BODY,{"disambiguationData":[OSD([makeQuery(id+"F0.imprint","IMPRINT",FACE,{"disambiguationData":[TD([[makeQuery(id+"F0.imprint","IMPRINT",EDGE,{"derivedFrom":subQ3}),1.0]])]}),makeQuery(id+"F2.imprint","IMPRINT",FACE,{"disambiguationData":[TD([[makeQuery(id+"F2.imprint","IMPRINT",EDGE,{"derivedFrom":sQuery(id+"F2.wireOp",EDGE,"E14.trimOffspring")}),1.0]])]})])]}),"instanceName":"19"});}
            var Q23;
            {var subQ3=sQuery(id+"F0.wireOp",EDGE,"E12.29.0");Q23=makeQuery(id+"F7.opPattern","COPY",BODY,{"derivedFrom":makeQuery(id+"F3.opLoft","SWEPT_BODY",BODY,{"disambiguationData":[OSD([makeQuery(id+"F0.imprint","IMPRINT",FACE,{"disambiguationData":[TD([[makeQuery(id+"F0.imprint","IMPRINT",EDGE,{"derivedFrom":subQ3}),1.0]])]}),makeQuery(id+"F2.imprint","IMPRINT",FACE,{"disambiguationData":[TD([[makeQuery(id+"F2.imprint","IMPRINT",EDGE,{"derivedFrom":sQuery(id+"F2.wireOp",EDGE,"E14.trimOffspring")}),1.0]])]})])]}),"instanceName":"18"});}
            var Q24;
            {var subQ3=sQuery(id+"F0.wireOp",EDGE,"E12.29.0");Q24=makeQuery(id+"F7.opPattern","COPY",BODY,{"derivedFrom":makeQuery(id+"F3.opLoft","SWEPT_BODY",BODY,{"disambiguationData":[OSD([makeQuery(id+"F0.imprint","IMPRINT",FACE,{"disambiguationData":[TD([[makeQuery(id+"F0.imprint","IMPRINT",EDGE,{"derivedFrom":subQ3}),1.0]])]}),makeQuery(id+"F2.imprint","IMPRINT",FACE,{"disambiguationData":[TD([[makeQuery(id+"F2.imprint","IMPRINT",EDGE,{"derivedFrom":sQuery(id+"F2.wireOp",EDGE,"E14.trimOffspring")}),1.0]])]})])]}),"instanceName":"17"});}
            var Q25;
            {var subQ3=sQuery(id+"F0.wireOp",EDGE,"E12.29.0");Q25=makeQuery(id+"F7.opPattern","COPY",BODY,{"derivedFrom":makeQuery(id+"F3.opLoft","SWEPT_BODY",BODY,{"disambiguationData":[OSD([makeQuery(id+"F0.imprint","IMPRINT",FACE,{"disambiguationData":[TD([[makeQuery(id+"F0.imprint","IMPRINT",EDGE,{"derivedFrom":subQ3}),1.0]])]}),makeQuery(id+"F2.imprint","IMPRINT",FACE,{"disambiguationData":[TD([[makeQuery(id+"F2.imprint","IMPRINT",EDGE,{"derivedFrom":sQuery(id+"F2.wireOp",EDGE,"E14.trimOffspring")}),1.0]])]})])]}),"instanceName":"16"});}
            var Q26;
            {var subQ3=sQuery(id+"F0.wireOp",EDGE,"E12.29.0");Q26=makeQuery(id+"F7.opPattern","COPY",BODY,{"derivedFrom":makeQuery(id+"F3.opLoft","SWEPT_BODY",BODY,{"disambiguationData":[OSD([makeQuery(id+"F0.imprint","IMPRINT",FACE,{"disambiguationData":[TD([[makeQuery(id+"F0.imprint","IMPRINT",EDGE,{"derivedFrom":subQ3}),1.0]])]}),makeQuery(id+"F2.imprint","IMPRINT",FACE,{"disambiguationData":[TD([[makeQuery(id+"F2.imprint","IMPRINT",EDGE,{"derivedFrom":sQuery(id+"F2.wireOp",EDGE,"E14.trimOffspring")}),1.0]])]})])]}),"instanceName":"15"});}
            var Q27;
            {var subQ3=sQuery(id+"F0.wireOp",EDGE,"E12.29.0");Q27=makeQuery(id+"F7.opPattern","COPY",BODY,{"derivedFrom":makeQuery(id+"F3.opLoft","SWEPT_BODY",BODY,{"disambiguationData":[OSD([makeQuery(id+"F0.imprint","IMPRINT",FACE,{"disambiguationData":[TD([[makeQuery(id+"F0.imprint","IMPRINT",EDGE,{"derivedFrom":subQ3}),1.0]])]}),makeQuery(id+"F2.imprint","IMPRINT",FACE,{"disambiguationData":[TD([[makeQuery(id+"F2.imprint","IMPRINT",EDGE,{"derivedFrom":sQuery(id+"F2.wireOp",EDGE,"E14.trimOffspring")}),1.0]])]})])]}),"instanceName":"14"});}
            var Q28;
            {var subQ3=sQuery(id+"F0.wireOp",EDGE,"E12.29.0");Q28=makeQuery(id+"F7.opPattern","COPY",BODY,{"derivedFrom":makeQuery(id+"F3.opLoft","SWEPT_BODY",BODY,{"disambiguationData":[OSD([makeQuery(id+"F0.imprint","IMPRINT",FACE,{"disambiguationData":[TD([[makeQuery(id+"F0.imprint","IMPRINT",EDGE,{"derivedFrom":subQ3}),1.0]])]}),makeQuery(id+"F2.imprint","IMPRINT",FACE,{"disambiguationData":[TD([[makeQuery(id+"F2.imprint","IMPRINT",EDGE,{"derivedFrom":sQuery(id+"F2.wireOp",EDGE,"E14.trimOffspring")}),1.0]])]})])]}),"instanceName":"13"});}
            var Q29;
            {var subQ3=sQuery(id+"F0.wireOp",EDGE,"E12.29.0");Q29=makeQuery(id+"F7.opPattern","COPY",BODY,{"derivedFrom":makeQuery(id+"F3.opLoft","SWEPT_BODY",BODY,{"disambiguationData":[OSD([makeQuery(id+"F0.imprint","IMPRINT",FACE,{"disambiguationData":[TD([[makeQuery(id+"F0.imprint","IMPRINT",EDGE,{"derivedFrom":subQ3}),1.0]])]}),makeQuery(id+"F2.imprint","IMPRINT",FACE,{"disambiguationData":[TD([[makeQuery(id+"F2.imprint","IMPRINT",EDGE,{"derivedFrom":sQuery(id+"F2.wireOp",EDGE,"E14.trimOffspring")}),1.0]])]})])]}),"instanceName":"12"});}
            booleanBodies(context, id + "F8", {"operationType" : BooleanOperationType.UNION, "tools" : qUnion([Q0, Q1, Q2, Q3, Q4, Q5, Q6, Q7, Q8, Q9, Q10, Q11, Q12, Q13, Q14, Q15, Q16, Q17, Q18, Q19, Q20, Q21, Q22, Q23, Q24, Q25, Q26, Q27, Q28, Q29])});
        }
        {
            var Q0;
            {var subQ3=makeQuery(id+"F6.boolean.opBoolean","MERGE",FACE,{"derivedFrom":[makeQuery(id+"F3.opLoft","CAP_FACE",FACE,{"disambiguationData":[OSD([makeQuery(id+"F2.imprint","IMPRINT",FACE,{"disambiguationData":[TD([[makeQuery(id+"F2.imprint","IMPRINT",EDGE,{"derivedFrom":sQuery(id+"F2.wireOp",EDGE,"E14.trimOffspring")}),1.0]])]})])],"isStart":true}),makeQuery(id+"F6.opLoft","CAP_FACE",FACE,{"disambiguationData":[OSD([makeQuery(id+"F4.imprint","IMPRINT",FACE,{"disambiguationData":[TD([[makeQuery(id+"F4.imprint","IMPRINT",EDGE,{"derivedFrom":sQuery(id+"F4.wireOp",EDGE,"E25")}),1.0]])]})])],"isStart":true})]});Q0=makeQuery(id+"F8.opBoolean","MERGE",FACE,{"derivedFrom":[subQ3,makeQuery(id+"F7.opPattern","COPY",FACE,{"derivedFrom":subQ3,"instanceName":"1"}),makeQuery(id+"F7.opPattern","COPY",FACE,{"derivedFrom":subQ3,"instanceName":"2"}),makeQuery(id+"F7.opPattern","COPY",FACE,{"derivedFrom":subQ3,"instanceName":"3"}),makeQuery(id+"F7.opPattern","COPY",FACE,{"derivedFrom":subQ3,"instanceName":"4"}),makeQuery(id+"F7.opPattern","COPY",FACE,{"derivedFrom":subQ3,"instanceName":"5"}),makeQuery(id+"F7.opPattern","COPY",FACE,{"derivedFrom":subQ3,"instanceName":"6"}),makeQuery(id+"F7.opPattern","COPY",FACE,{"derivedFrom":subQ3,"instanceName":"7"}),makeQuery(id+"F7.opPattern","COPY",FACE,{"derivedFrom":subQ3,"instanceName":"8"}),makeQuery(id+"F7.opPattern","COPY",FACE,{"derivedFrom":subQ3,"instanceName":"9"}),makeQuery(id+"F7.opPattern","COPY",FACE,{"derivedFrom":subQ3,"instanceName":"10"}),makeQuery(id+"F7.opPattern","COPY",FACE,{"derivedFrom":subQ3,"instanceName":"11"}),makeQuery(id+"F7.opPattern","COPY",FACE,{"derivedFrom":subQ3,"instanceName":"12"}),makeQuery(id+"F7.opPattern","COPY",FACE,{"derivedFrom":subQ3,"instanceName":"13"}),makeQuery(id+"F7.opPattern","COPY",FACE,{"derivedFrom":subQ3,"instanceName":"14"}),makeQuery(id+"F7.opPattern","COPY",FACE,{"derivedFrom":subQ3,"instanceName":"15"}),makeQuery(id+"F7.opPattern","COPY",FACE,{"derivedFrom":subQ3,"instanceName":"16"}),makeQuery(id+"F7.opPattern","COPY",FACE,{"derivedFrom":subQ3,"instanceName":"17"}),makeQuery(id+"F7.opPattern","COPY",FACE,{"derivedFrom":subQ3,"instanceName":"18"}),makeQuery(id+"F7.opPattern","COPY",FACE,{"derivedFrom":subQ3,"instanceName":"19"}),makeQuery(id+"F7.opPattern","COPY",FACE,{"derivedFrom":subQ3,"instanceName":"20"}),makeQuery(id+"F7.opPattern","COPY",FACE,{"derivedFrom":subQ3,"instanceName":"21"}),makeQuery(id+"F7.opPattern","COPY",FACE,{"derivedFrom":subQ3,"instanceName":"22"}),makeQuery(id+"F7.opPattern","COPY",FACE,{"derivedFrom":subQ3,"instanceName":"23"}),makeQuery(id+"F7.opPattern","COPY",FACE,{"derivedFrom":subQ3,"instanceName":"24"}),makeQuery(id+"F7.opPattern","COPY",FACE,{"derivedFrom":subQ3,"instanceName":"25"}),makeQuery(id+"F7.opPattern","COPY",FACE,{"derivedFrom":subQ3,"instanceName":"26"}),makeQuery(id+"F7.opPattern","COPY",FACE,{"derivedFrom":subQ3,"instanceName":"27"}),makeQuery(id+"F7.opPattern","COPY",FACE,{"derivedFrom":subQ3,"instanceName":"28"}),makeQuery(id+"F7.opPattern","COPY",FACE,{"derivedFrom":subQ3,"instanceName":"29"})]});}
            var sketch = newSketch(context, id + "F9", { "sketchPlane" : qUnion([Q0])});
            skPoint(sketch, "E27", {"position": v(0, 0) * mm});
            skSolve(sketch);
        }
        {
            var Q0;
            Q0=sQuery(id+"F9.wireOp",VERTEX,"E27");
            var Q1;
            {var subQ3=sQuery(id+"F0.wireOp",EDGE,"E12.29.0");Q1=makeQuery(id+"F7.opPattern","COPY",BODY,{"derivedFrom":makeQuery(id+"F3.opLoft","SWEPT_BODY",BODY,{"disambiguationData":[OSD([makeQuery(id+"F0.imprint","IMPRINT",FACE,{"disambiguationData":[TD([[makeQuery(id+"F0.imprint","IMPRINT",EDGE,{"derivedFrom":subQ3}),1.0]])]}),makeQuery(id+"F2.imprint","IMPRINT",FACE,{"disambiguationData":[TD([[makeQuery(id+"F2.imprint","IMPRINT",EDGE,{"derivedFrom":sQuery(id+"F2.wireOp",EDGE,"E14.trimOffspring")}),1.0]])]})])]}),"instanceName":"11"});}
            hole(context, id + "F10", {"style" : HoleStyle.SIMPLE, "endStyle" : HoleEndStyle.THROUGH, "holeDiameter" : 12.7 * mm, "tappedDepth" : 12.7 * mm, "tapClearance" : 3, "locations" : qUnion([Q0]), "scope" : qUnion([Q1])});
        }
    });
